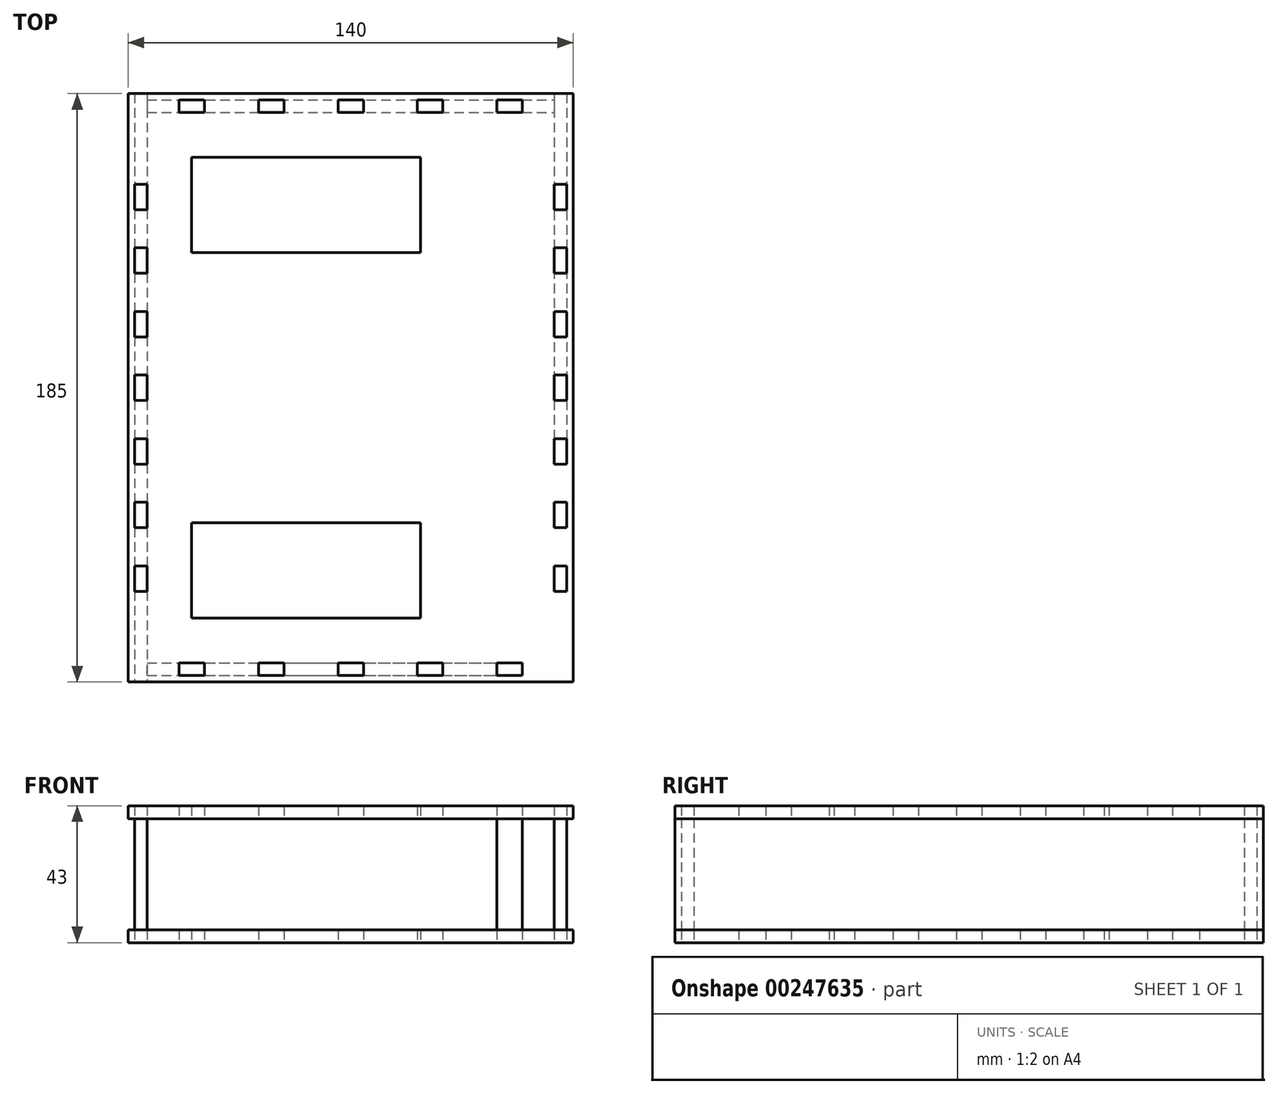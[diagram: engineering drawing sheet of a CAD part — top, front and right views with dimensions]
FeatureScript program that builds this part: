
annotation { "Feature Type Name" : "Feature", "Feature Type Description" : "" }
export const myFeature = defineFeature(function(context is Context, id is Id, definition is map)
    precondition{}
    {
        {
            var Q0;
            Q0=qCreatedBy(makeId("Top.planeOp"),FACE);
            var sketch = newSketch(context, id + "F0", { "sketchPlane" : qUnion([Q0])});
            skLineSegment(sketch, "E0.bottom", {"start": v(70, -92.5) * mm, "end": v(-70, -92.5) * mm});
            skLineSegment(sketch, "E0.top", {"start": v(70, 92.5) * mm, "end": v(-70, 92.5) * mm});
            skLineSegment(sketch, "E0.left", {"start": v(70, -92.5) * mm, "end": v(70, 92.5) * mm});
            skLineSegment(sketch, "E0.right", {"start": v(-70, -92.5) * mm, "end": v(-70, 92.5) * mm});
            skPoint(sketch, "E0.middle", {"position": v(0, 0) * mm});
            skPoint(sketch, "E1", {"position": v(0, 90.5) * mm});
            skLineSegment(sketch, "E2.bottom", {"start": v(0, 90.5) * mm, "end": v(4, 90.5) * mm});
            skLineSegment(sketch, "E2.top", {"start": v(0, 86.5) * mm, "end": v(4, 86.5) * mm});
            skLineSegment(sketch, "E2.left", {"start": v(0, 90.5) * mm, "end": v(0, 86.5) * mm});
            skLineSegment(sketch, "E2.right", {"start": v(4, 90.5) * mm, "end": v(4, 86.5) * mm});
            skLineSegment(sketch, "E3.MirrorCS", {"start": v(-4, 90.5) * mm, "end": v(-4, 86.5) * mm});
            skLineSegment(sketch, "E4.MirrorCS", {"start": v(0, 90.5) * mm, "end": v(-4, 90.5) * mm});
            skLineSegment(sketch, "E5.MirrorCS", {"start": v(0, 86.5) * mm, "end": v(-4, 86.5) * mm});
            skLineSegment(sketch, "E6.1.0.0", {"start": v(25, 86.5) * mm, "end": v(21, 86.5) * mm});
            skLineSegment(sketch, "E6.1.0.1", {"start": v(21, 90.5) * mm, "end": v(21, 86.5) * mm});
            skLineSegment(sketch, "E6.1.0.2", {"start": v(25, 90.5) * mm, "end": v(21, 90.5) * mm});
            skLineSegment(sketch, "E6.1.0.3", {"start": v(25, 90.5) * mm, "end": v(29, 90.5) * mm});
            skLineSegment(sketch, "E6.1.0.4", {"start": v(25, 86.5) * mm, "end": v(29, 86.5) * mm});
            skLineSegment(sketch, "E6.1.0.5", {"start": v(29, 90.5) * mm, "end": v(29, 86.5) * mm});
            skLineSegment(sketch, "E6.2.0.0", {"start": v(50, 86.5) * mm, "end": v(46, 86.5) * mm});
            skLineSegment(sketch, "E6.2.0.1", {"start": v(46, 90.5) * mm, "end": v(46, 86.5) * mm});
            skLineSegment(sketch, "E6.2.0.2", {"start": v(50, 90.5) * mm, "end": v(46, 90.5) * mm});
            skLineSegment(sketch, "E6.2.0.3", {"start": v(50, 90.5) * mm, "end": v(54, 90.5) * mm});
            skLineSegment(sketch, "E6.2.0.4", {"start": v(50, 86.5) * mm, "end": v(54, 86.5) * mm});
            skLineSegment(sketch, "E6.2.0.5", {"start": v(54, 90.5) * mm, "end": v(54, 86.5) * mm});
            skLineSegment(sketch, "E6.direction1", {"start": v(-4, 86.5) * mm, "end": v(21, 86.5) * mm, "construction": true});
            skLineSegment(sketch, "E7.MirrorCS", {"start": v(-25, 90.5) * mm, "end": v(-21, 90.5) * mm});
            skLineSegment(sketch, "E8.MirrorCS", {"start": v(-25, 90.5) * mm, "end": v(-29, 90.5) * mm});
            skLineSegment(sketch, "E9.MirrorCS", {"start": v(-29, 90.5) * mm, "end": v(-29, 86.5) * mm});
            skLineSegment(sketch, "E10.MirrorCS", {"start": v(-21, 90.5) * mm, "end": v(-21, 86.5) * mm});
            skLineSegment(sketch, "E11.MirrorCS", {"start": v(-25, 86.5) * mm, "end": v(-21, 86.5) * mm});
            skLineSegment(sketch, "E12.MirrorCS", {"start": v(-25, 86.5) * mm, "end": v(-29, 86.5) * mm});
            skLineSegment(sketch, "E13.MirrorCS", {"start": v(-50, 90.5) * mm, "end": v(-46, 90.5) * mm});
            skLineSegment(sketch, "E14.MirrorCS", {"start": v(-50, 90.5) * mm, "end": v(-54, 90.5) * mm});
            skLineSegment(sketch, "E15.MirrorCS", {"start": v(-54, 90.5) * mm, "end": v(-54, 86.5) * mm});
            skLineSegment(sketch, "E16.MirrorCS", {"start": v(-50, 86.5) * mm, "end": v(-54, 86.5) * mm});
            skLineSegment(sketch, "E17.MirrorCS", {"start": v(-50, 86.5) * mm, "end": v(-46, 86.5) * mm});
            skLineSegment(sketch, "E18.MirrorCS", {"start": v(-46, 90.5) * mm, "end": v(-46, 86.5) * mm});
            skLineSegment(sketch, "E19", {"start": v(-70, 0) * mm, "end": v(70, 0) * mm, "construction": true});
            skPoint(sketch, "E20", {"position": v(-68, 0) * mm});
            skLineSegment(sketch, "E21.bottom", {"start": v(-68, 0) * mm, "end": v(-64, 0) * mm});
            skLineSegment(sketch, "E21.top", {"start": v(-68, 4) * mm, "end": v(-64, 4) * mm});
            skLineSegment(sketch, "E21.left", {"start": v(-68, 0) * mm, "end": v(-68, 4) * mm});
            skLineSegment(sketch, "E21.right", {"start": v(-64, 0) * mm, "end": v(-64, 4) * mm});
            skLineSegment(sketch, "E22.MirrorCS", {"start": v(-68, -4) * mm, "end": v(-64, -4) * mm});
            skLineSegment(sketch, "E23.MirrorCS", {"start": v(-68, 0) * mm, "end": v(-68, -4) * mm});
            skLineSegment(sketch, "E24.MirrorCS", {"start": v(-64, 0) * mm, "end": v(-64, -4) * mm});
            skLineSegment(sketch, "E25.0.1.0", {"start": v(-68, 24) * mm, "end": v(-64, 24) * mm});
            skLineSegment(sketch, "E25.0.1.1", {"start": v(-68, 20) * mm, "end": v(-68, 24) * mm});
            skLineSegment(sketch, "E25.0.1.2", {"start": v(-64, 20) * mm, "end": v(-64, 24) * mm});
            skLineSegment(sketch, "E25.0.1.3", {"start": v(-64, 20) * mm, "end": v(-64, 16) * mm});
            skLineSegment(sketch, "E25.0.1.4", {"start": v(-68, 16) * mm, "end": v(-64, 16) * mm});
            skLineSegment(sketch, "E25.0.1.5", {"start": v(-68, 20) * mm, "end": v(-68, 16) * mm});
            skLineSegment(sketch, "E25.0.2.0", {"start": v(-68, 44) * mm, "end": v(-64, 44) * mm});
            skLineSegment(sketch, "E25.0.2.1", {"start": v(-68, 40) * mm, "end": v(-68, 44) * mm});
            skLineSegment(sketch, "E25.0.2.2", {"start": v(-64, 40) * mm, "end": v(-64, 44) * mm});
            skLineSegment(sketch, "E25.0.2.3", {"start": v(-64, 40) * mm, "end": v(-64, 36) * mm});
            skLineSegment(sketch, "E25.0.2.4", {"start": v(-68, 36) * mm, "end": v(-64, 36) * mm});
            skLineSegment(sketch, "E25.0.2.5", {"start": v(-68, 40) * mm, "end": v(-68, 36) * mm});
            skLineSegment(sketch, "E25.0.3.0", {"start": v(-68, 64) * mm, "end": v(-64, 64) * mm});
            skLineSegment(sketch, "E25.0.3.1", {"start": v(-68, 60) * mm, "end": v(-68, 64) * mm});
            skLineSegment(sketch, "E25.0.3.2", {"start": v(-64, 60) * mm, "end": v(-64, 64) * mm});
            skLineSegment(sketch, "E25.0.3.3", {"start": v(-64, 60) * mm, "end": v(-64, 56) * mm});
            skLineSegment(sketch, "E25.0.3.4", {"start": v(-68, 56) * mm, "end": v(-64, 56) * mm});
            skLineSegment(sketch, "E25.0.3.5", {"start": v(-68, 60) * mm, "end": v(-68, 56) * mm});
            skLineSegment(sketch, "E25.direction1", {"start": v(-68, 4) * mm, "end": v(-43, 4) * mm, "construction": true});
            skLineSegment(sketch, "E25.direction2", {"start": v(-68, 4) * mm, "end": v(-68, 24) * mm, "construction": true});
            skLineSegment(sketch, "E26.MirrorCS", {"start": v(-68, -24) * mm, "end": v(-64, -24) * mm});
            skLineSegment(sketch, "E27.MirrorCS", {"start": v(-64, -20) * mm, "end": v(-64, -24) * mm});
            skLineSegment(sketch, "E28.MirrorCS", {"start": v(-64, -20) * mm, "end": v(-64, -16) * mm});
            skLineSegment(sketch, "E29.MirrorCS", {"start": v(-68, -16) * mm, "end": v(-64, -16) * mm});
            skLineSegment(sketch, "E30.MirrorCS", {"start": v(-68, -36) * mm, "end": v(-64, -36) * mm});
            skLineSegment(sketch, "E31.MirrorCS", {"start": v(-68, -40) * mm, "end": v(-68, -36) * mm});
            skLineSegment(sketch, "E32.MirrorCS", {"start": v(-68, -40) * mm, "end": v(-68, -44) * mm});
            skLineSegment(sketch, "E33.MirrorCS", {"start": v(-68, -44) * mm, "end": v(-64, -44) * mm});
            skLineSegment(sketch, "E34.MirrorCS", {"start": v(-64, -40) * mm, "end": v(-64, -44) * mm});
            skLineSegment(sketch, "E35.MirrorCS", {"start": v(-64, -40) * mm, "end": v(-64, -36) * mm});
            skLineSegment(sketch, "E36.MirrorCS", {"start": v(-68, -64) * mm, "end": v(-64, -64) * mm});
            skLineSegment(sketch, "E37.MirrorCS", {"start": v(-68, -60) * mm, "end": v(-68, -64) * mm});
            skLineSegment(sketch, "E38.MirrorCS", {"start": v(-64, -60) * mm, "end": v(-64, -64) * mm});
            skLineSegment(sketch, "E39.MirrorCS", {"start": v(-64, -60) * mm, "end": v(-64, -56) * mm});
            skLineSegment(sketch, "E40.MirrorCS", {"start": v(-68, -60) * mm, "end": v(-68, -56) * mm});
            skLineSegment(sketch, "E41.MirrorCS", {"start": v(-68, -56) * mm, "end": v(-64, -56) * mm});
            skLineSegment(sketch, "E42", {"start": v(-68, -16) * mm, "end": v(-68, -24) * mm});
            skLineSegment(sketch, "E43.MirrorCS", {"start": v(68, 64) * mm, "end": v(64, 64) * mm});
            skLineSegment(sketch, "E44.MirrorCS", {"start": v(64, 60) * mm, "end": v(64, 64) * mm});
            skLineSegment(sketch, "E45.MirrorCS", {"start": v(68, 60) * mm, "end": v(68, 64) * mm});
            skLineSegment(sketch, "E46.MirrorCS", {"start": v(68, 60) * mm, "end": v(68, 56) * mm});
            skLineSegment(sketch, "E47.MirrorCS", {"start": v(64, 60) * mm, "end": v(64, 56) * mm});
            skLineSegment(sketch, "E48.MirrorCS", {"start": v(68, 56) * mm, "end": v(64, 56) * mm});
            skLineSegment(sketch, "E49.MirrorCS", {"start": v(68, 44) * mm, "end": v(64, 44) * mm});
            skLineSegment(sketch, "E50.MirrorCS", {"start": v(64, 40) * mm, "end": v(64, 44) * mm});
            skLineSegment(sketch, "E51.MirrorCS", {"start": v(64, 40) * mm, "end": v(64, 36) * mm});
            skLineSegment(sketch, "E52.MirrorCS", {"start": v(68, 36) * mm, "end": v(64, 36) * mm});
            skLineSegment(sketch, "E53.MirrorCS", {"start": v(68, 40) * mm, "end": v(68, 36) * mm});
            skLineSegment(sketch, "E54.MirrorCS", {"start": v(68, 40) * mm, "end": v(68, 44) * mm});
            skLineSegment(sketch, "E55.MirrorCS", {"start": v(68, 24) * mm, "end": v(64, 24) * mm});
            skLineSegment(sketch, "E56.MirrorCS", {"start": v(64, 20) * mm, "end": v(64, 24) * mm});
            skLineSegment(sketch, "E57.MirrorCS", {"start": v(64, 20) * mm, "end": v(64, 16) * mm});
            skLineSegment(sketch, "E58.MirrorCS", {"start": v(68, 16) * mm, "end": v(64, 16) * mm});
            skLineSegment(sketch, "E59.MirrorCS", {"start": v(68, 0) * mm, "end": v(68, 4) * mm});
            skLineSegment(sketch, "E60.MirrorCS", {"start": v(68, 0) * mm, "end": v(68, -4) * mm});
            skLineSegment(sketch, "E61.MirrorCS", {"start": v(68, -4) * mm, "end": v(64, -4) * mm});
            skLineSegment(sketch, "E62.MirrorCS", {"start": v(64, 0) * mm, "end": v(64, -4) * mm});
            skLineSegment(sketch, "E63.MirrorCS", {"start": v(64, 0) * mm, "end": v(64, 4) * mm});
            skLineSegment(sketch, "E64.MirrorCS", {"start": v(68, -16) * mm, "end": v(64, -16) * mm});
            skLineSegment(sketch, "E65.MirrorCS", {"start": v(68, -16) * mm, "end": v(68, -24) * mm});
            skLineSegment(sketch, "E66.MirrorCS", {"start": v(64, -20) * mm, "end": v(64, -16) * mm});
            skLineSegment(sketch, "E67.MirrorCS", {"start": v(64, -20) * mm, "end": v(64, -24) * mm});
            skLineSegment(sketch, "E68.MirrorCS", {"start": v(68, -24) * mm, "end": v(64, -24) * mm});
            skLineSegment(sketch, "E69.MirrorCS", {"start": v(68, -36) * mm, "end": v(64, -36) * mm});
            skLineSegment(sketch, "E70.MirrorCS", {"start": v(68, -40) * mm, "end": v(68, -36) * mm});
            skLineSegment(sketch, "E71.MirrorCS", {"start": v(64, -40) * mm, "end": v(64, -36) * mm});
            skLineSegment(sketch, "E72.MirrorCS", {"start": v(64, -40) * mm, "end": v(64, -44) * mm});
            skLineSegment(sketch, "E73.MirrorCS", {"start": v(68, -40) * mm, "end": v(68, -44) * mm});
            skLineSegment(sketch, "E74.MirrorCS", {"start": v(68, -44) * mm, "end": v(64, -44) * mm});
            skLineSegment(sketch, "E75.MirrorCS", {"start": v(68, -56) * mm, "end": v(64, -56) * mm});
            skLineSegment(sketch, "E76.MirrorCS", {"start": v(68, -60) * mm, "end": v(68, -56) * mm});
            skLineSegment(sketch, "E77.MirrorCS", {"start": v(64, -60) * mm, "end": v(64, -56) * mm});
            skLineSegment(sketch, "E78.MirrorCS", {"start": v(64, -60) * mm, "end": v(64, -64) * mm});
            skLineSegment(sketch, "E79.MirrorCS", {"start": v(68, -64) * mm, "end": v(64, -64) * mm});
            skLineSegment(sketch, "E80.MirrorCS", {"start": v(68, -60) * mm, "end": v(68, -64) * mm});
            skLineSegment(sketch, "E81", {"start": v(64, 4) * mm, "end": v(68, 4) * mm});
            skLineSegment(sketch, "E82", {"start": v(68, 24) * mm, "end": v(68, 16) * mm});
            skLineSegment(sketch, "E83.MirrorCS", {"start": v(-50, -90.5) * mm, "end": v(-54, -90.5) * mm});
            skLineSegment(sketch, "E84.MirrorCS", {"start": v(-50, -90.5) * mm, "end": v(-46, -90.5) * mm});
            skLineSegment(sketch, "E85.MirrorCS", {"start": v(-46, -90.5) * mm, "end": v(-46, -86.5) * mm});
            skLineSegment(sketch, "E86.MirrorCS", {"start": v(-50, -86.5) * mm, "end": v(-46, -86.5) * mm});
            skLineSegment(sketch, "E87.MirrorCS", {"start": v(-50, -86.5) * mm, "end": v(-54, -86.5) * mm});
            skLineSegment(sketch, "E88.MirrorCS", {"start": v(-54, -90.5) * mm, "end": v(-54, -86.5) * mm});
            skLineSegment(sketch, "E89.MirrorCS", {"start": v(-25, -90.5) * mm, "end": v(-29, -90.5) * mm});
            skLineSegment(sketch, "E90.MirrorCS", {"start": v(-25, -90.5) * mm, "end": v(-21, -90.5) * mm});
            skLineSegment(sketch, "E91.MirrorCS", {"start": v(-21, -90.5) * mm, "end": v(-21, -86.5) * mm});
            skLineSegment(sketch, "E92.MirrorCS", {"start": v(-25, -86.5) * mm, "end": v(-21, -86.5) * mm});
            skLineSegment(sketch, "E93.MirrorCS", {"start": v(-25, -86.5) * mm, "end": v(-29, -86.5) * mm});
            skLineSegment(sketch, "E94.MirrorCS", {"start": v(-29, -90.5) * mm, "end": v(-29, -86.5) * mm});
            skLineSegment(sketch, "E95.MirrorCS", {"start": v(0, -90.5) * mm, "end": v(-4, -90.5) * mm});
            skLineSegment(sketch, "E96.MirrorCS", {"start": v(0, -90.5) * mm, "end": v(4, -90.5) * mm});
            skLineSegment(sketch, "E97.MirrorCS", {"start": v(4, -90.5) * mm, "end": v(4, -86.5) * mm});
            skLineSegment(sketch, "E98.MirrorCS", {"start": v(-4, -90.5) * mm, "end": v(-4, -86.5) * mm});
            skLineSegment(sketch, "E99.MirrorCS", {"start": v(25, -90.5) * mm, "end": v(21, -90.5) * mm});
            skLineSegment(sketch, "E100.MirrorCS", {"start": v(25, -90.5) * mm, "end": v(29, -90.5) * mm});
            skLineSegment(sketch, "E101.MirrorCS", {"start": v(29, -90.5) * mm, "end": v(29, -86.5) * mm});
            skLineSegment(sketch, "E102.MirrorCS", {"start": v(25, -86.5) * mm, "end": v(29, -86.5) * mm});
            skLineSegment(sketch, "E103.MirrorCS", {"start": v(25, -86.5) * mm, "end": v(21, -86.5) * mm});
            skLineSegment(sketch, "E104.MirrorCS", {"start": v(21, -90.5) * mm, "end": v(21, -86.5) * mm});
            skLineSegment(sketch, "E105.MirrorCS", {"start": v(50, -90.5) * mm, "end": v(46, -90.5) * mm});
            skLineSegment(sketch, "E106.MirrorCS", {"start": v(50, -90.5) * mm, "end": v(54, -90.5) * mm});
            skLineSegment(sketch, "E107.MirrorCS", {"start": v(54, -90.5) * mm, "end": v(54, -86.5) * mm});
            skLineSegment(sketch, "E108.MirrorCS", {"start": v(50, -86.5) * mm, "end": v(54, -86.5) * mm});
            skLineSegment(sketch, "E109.MirrorCS", {"start": v(50, -86.5) * mm, "end": v(46, -86.5) * mm});
            skLineSegment(sketch, "E110.MirrorCS", {"start": v(46, -90.5) * mm, "end": v(46, -86.5) * mm});
            skLineSegment(sketch, "E111", {"start": v(-4, -86.5) * mm, "end": v(4, -86.5) * mm});
            skLineSegment(sketch, "E112", {"start": v(-50, -42.5) * mm, "end": v(-50, -72.5) * mm});
            skLineSegment(sketch, "E113", {"start": v(22, -42.5) * mm, "end": v(22, -72.5) * mm});
            skLineSegment(sketch, "E114", {"start": v(-50, -42.5) * mm, "end": v(22, -42.5) * mm});
            skLineSegment(sketch, "E115", {"start": v(-50, -72.5) * mm, "end": v(22, -72.5) * mm});
            skLineSegment(sketch, "E116", {"start": v(0, -92.5) * mm, "end": v(0, 92.5) * mm, "construction": true});
            skLineSegment(sketch, "E117.MirrorCS", {"start": v(-50, 42.5) * mm, "end": v(-50, 72.5) * mm});
            skLineSegment(sketch, "E118.MirrorCS", {"start": v(-50, 72.5) * mm, "end": v(22, 72.5) * mm});
            skLineSegment(sketch, "E119.MirrorCS", {"start": v(-50, 42.5) * mm, "end": v(22, 42.5) * mm});
            skLineSegment(sketch, "E120.MirrorCS", {"start": v(22, 42.5) * mm, "end": v(22, 72.5) * mm});
            skSolve(sketch);
        }
        {
            var Q0;
            Q0=makeQuery(id+"F0.imprint","IMPRINT",FACE,{"disambiguationData":[TD([[makeQuery(id+"F0.imprint","IMPRINT",EDGE,{"derivedFrom":sQuery(id+"F0.wireOp",EDGE,"E0.bottom")}),-1.0]])]});
            extrude(context, id + "F1", {"entities" : qUnion([Q0]), "depth" : 4 * mm});
        }
        {
            var Q0;
            Q0=makeQuery(id+"F1.opExtrude","CAP_FACE",FACE,{"disambiguationData":[OSD([sQuery(id+"F0.wireOp",EDGE,"E0.bottom"),sQuery(id+"F0.wireOp",EDGE,"E0.top"),sQuery(id+"F0.wireOp",EDGE,"E0.left"),sQuery(id+"F0.wireOp",EDGE,"E0.right"),sQuery(id+"F0.wireOp",EDGE,"E2.bottom"),sQuery(id+"F0.wireOp",EDGE,"E2.top"),sQuery(id+"F0.wireOp",EDGE,"E2.right"),sQuery(id+"F0.wireOp",EDGE,"E3.MirrorCS"),sQuery(id+"F0.wireOp",EDGE,"E4.MirrorCS"),sQuery(id+"F0.wireOp",EDGE,"E5.MirrorCS"),sQuery(id+"F0.wireOp",EDGE,"E6.1.0.0"),sQuery(id+"F0.wireOp",EDGE,"E6.1.0.1"),sQuery(id+"F0.wireOp",EDGE,"E6.1.0.2"),sQuery(id+"F0.wireOp",EDGE,"E6.1.0.3"),sQuery(id+"F0.wireOp",EDGE,"E6.1.0.4"),sQuery(id+"F0.wireOp",EDGE,"E6.1.0.5"),sQuery(id+"F0.wireOp",EDGE,"E6.2.0.0"),sQuery(id+"F0.wireOp",EDGE,"E6.2.0.1"),sQuery(id+"F0.wireOp",EDGE,"E6.2.0.2"),sQuery(id+"F0.wireOp",EDGE,"E6.2.0.3"),sQuery(id+"F0.wireOp",EDGE,"E6.2.0.4"),sQuery(id+"F0.wireOp",EDGE,"E6.2.0.5"),sQuery(id+"F0.wireOp",EDGE,"E7.MirrorCS"),sQuery(id+"F0.wireOp",EDGE,"E8.MirrorCS"),sQuery(id+"F0.wireOp",EDGE,"E9.MirrorCS"),sQuery(id+"F0.wireOp",EDGE,"E10.MirrorCS"),sQuery(id+"F0.wireOp",EDGE,"E11.MirrorCS"),sQuery(id+"F0.wireOp",EDGE,"E12.MirrorCS"),sQuery(id+"F0.wireOp",EDGE,"E13.MirrorCS"),sQuery(id+"F0.wireOp",EDGE,"E14.MirrorCS"),sQuery(id+"F0.wireOp",EDGE,"E15.MirrorCS"),sQuery(id+"F0.wireOp",EDGE,"E16.MirrorCS"),sQuery(id+"F0.wireOp",EDGE,"E17.MirrorCS"),sQuery(id+"F0.wireOp",EDGE,"E18.MirrorCS"),sQuery(id+"F0.wireOp",EDGE,"E21.top"),sQuery(id+"F0.wireOp",EDGE,"E21.left"),sQuery(id+"F0.wireOp",EDGE,"E21.right"),sQuery(id+"F0.wireOp",EDGE,"E22.MirrorCS"),sQuery(id+"F0.wireOp",EDGE,"E23.MirrorCS"),sQuery(id+"F0.wireOp",EDGE,"E24.MirrorCS"),sQuery(id+"F0.wireOp",EDGE,"E25.0.1.0"),sQuery(id+"F0.wireOp",EDGE,"E25.0.1.1"),sQuery(id+"F0.wireOp",EDGE,"E25.0.1.2"),sQuery(id+"F0.wireOp",EDGE,"E25.0.1.3"),sQuery(id+"F0.wireOp",EDGE,"E25.0.1.4"),sQuery(id+"F0.wireOp",EDGE,"E25.0.1.5"),sQuery(id+"F0.wireOp",EDGE,"E25.0.2.0"),sQuery(id+"F0.wireOp",EDGE,"E25.0.2.1"),sQuery(id+"F0.wireOp",EDGE,"E25.0.2.2"),sQuery(id+"F0.wireOp",EDGE,"E25.0.2.3"),sQuery(id+"F0.wireOp",EDGE,"E25.0.2.4"),sQuery(id+"F0.wireOp",EDGE,"E25.0.2.5"),sQuery(id+"F0.wireOp",EDGE,"E25.0.3.0"),sQuery(id+"F0.wireOp",EDGE,"E25.0.3.1"),sQuery(id+"F0.wireOp",EDGE,"E25.0.3.2"),sQuery(id+"F0.wireOp",EDGE,"E25.0.3.3"),sQuery(id+"F0.wireOp",EDGE,"E25.0.3.4"),sQuery(id+"F0.wireOp",EDGE,"E25.0.3.5"),sQuery(id+"F0.wireOp",EDGE,"E26.MirrorCS"),sQuery(id+"F0.wireOp",EDGE,"E27.MirrorCS"),sQuery(id+"F0.wireOp",EDGE,"E28.MirrorCS"),sQuery(id+"F0.wireOp",EDGE,"E29.MirrorCS"),sQuery(id+"F0.wireOp",EDGE,"E30.MirrorCS"),sQuery(id+"F0.wireOp",EDGE,"E31.MirrorCS"),sQuery(id+"F0.wireOp",EDGE,"E32.MirrorCS"),sQuery(id+"F0.wireOp",EDGE,"E33.MirrorCS"),sQuery(id+"F0.wireOp",EDGE,"E34.MirrorCS"),sQuery(id+"F0.wireOp",EDGE,"E35.MirrorCS"),sQuery(id+"F0.wireOp",EDGE,"E36.MirrorCS"),sQuery(id+"F0.wireOp",EDGE,"E37.MirrorCS"),sQuery(id+"F0.wireOp",EDGE,"E38.MirrorCS"),sQuery(id+"F0.wireOp",EDGE,"E39.MirrorCS"),sQuery(id+"F0.wireOp",EDGE,"E40.MirrorCS"),sQuery(id+"F0.wireOp",EDGE,"E41.MirrorCS"),sQuery(id+"F0.wireOp",EDGE,"E42"),sQuery(id+"F0.wireOp",EDGE,"E43.MirrorCS"),sQuery(id+"F0.wireOp",EDGE,"E44.MirrorCS"),sQuery(id+"F0.wireOp",EDGE,"E45.MirrorCS"),sQuery(id+"F0.wireOp",EDGE,"E46.MirrorCS"),sQuery(id+"F0.wireOp",EDGE,"E47.MirrorCS"),sQuery(id+"F0.wireOp",EDGE,"E48.MirrorCS"),sQuery(id+"F0.wireOp",EDGE,"E49.MirrorCS"),sQuery(id+"F0.wireOp",EDGE,"E50.MirrorCS"),sQuery(id+"F0.wireOp",EDGE,"E51.MirrorCS"),sQuery(id+"F0.wireOp",EDGE,"E52.MirrorCS"),sQuery(id+"F0.wireOp",EDGE,"E53.MirrorCS"),sQuery(id+"F0.wireOp",EDGE,"E54.MirrorCS"),sQuery(id+"F0.wireOp",EDGE,"E55.MirrorCS"),sQuery(id+"F0.wireOp",EDGE,"E56.MirrorCS"),sQuery(id+"F0.wireOp",EDGE,"E57.MirrorCS"),sQuery(id+"F0.wireOp",EDGE,"E58.MirrorCS"),sQuery(id+"F0.wireOp",EDGE,"E59.MirrorCS"),sQuery(id+"F0.wireOp",EDGE,"E60.MirrorCS"),sQuery(id+"F0.wireOp",EDGE,"E61.MirrorCS"),sQuery(id+"F0.wireOp",EDGE,"E62.MirrorCS"),sQuery(id+"F0.wireOp",EDGE,"E63.MirrorCS"),sQuery(id+"F0.wireOp",EDGE,"E64.MirrorCS"),sQuery(id+"F0.wireOp",EDGE,"E65.MirrorCS"),sQuery(id+"F0.wireOp",EDGE,"E66.MirrorCS"),sQuery(id+"F0.wireOp",EDGE,"E67.MirrorCS"),sQuery(id+"F0.wireOp",EDGE,"E68.MirrorCS"),sQuery(id+"F0.wireOp",EDGE,"E69.MirrorCS"),sQuery(id+"F0.wireOp",EDGE,"E70.MirrorCS"),sQuery(id+"F0.wireOp",EDGE,"E71.MirrorCS"),sQuery(id+"F0.wireOp",EDGE,"E72.MirrorCS"),sQuery(id+"F0.wireOp",EDGE,"E73.MirrorCS"),sQuery(id+"F0.wireOp",EDGE,"E74.MirrorCS"),sQuery(id+"F0.wireOp",EDGE,"E75.MirrorCS"),sQuery(id+"F0.wireOp",EDGE,"E76.MirrorCS"),sQuery(id+"F0.wireOp",EDGE,"E77.MirrorCS"),sQuery(id+"F0.wireOp",EDGE,"E78.MirrorCS"),sQuery(id+"F0.wireOp",EDGE,"E79.MirrorCS"),sQuery(id+"F0.wireOp",EDGE,"E80.MirrorCS"),sQuery(id+"F0.wireOp",EDGE,"E81"),sQuery(id+"F0.wireOp",EDGE,"E82"),sQuery(id+"F0.wireOp",EDGE,"E83.MirrorCS"),sQuery(id+"F0.wireOp",EDGE,"E84.MirrorCS"),sQuery(id+"F0.wireOp",EDGE,"E85.MirrorCS"),sQuery(id+"F0.wireOp",EDGE,"E86.MirrorCS"),sQuery(id+"F0.wireOp",EDGE,"E87.MirrorCS"),sQuery(id+"F0.wireOp",EDGE,"E88.MirrorCS"),sQuery(id+"F0.wireOp",EDGE,"E89.MirrorCS"),sQuery(id+"F0.wireOp",EDGE,"E90.MirrorCS"),sQuery(id+"F0.wireOp",EDGE,"E91.MirrorCS"),sQuery(id+"F0.wireOp",EDGE,"E92.MirrorCS"),sQuery(id+"F0.wireOp",EDGE,"E93.MirrorCS"),sQuery(id+"F0.wireOp",EDGE,"E94.MirrorCS"),sQuery(id+"F0.wireOp",EDGE,"E95.MirrorCS"),sQuery(id+"F0.wireOp",EDGE,"E96.MirrorCS"),sQuery(id+"F0.wireOp",EDGE,"E97.MirrorCS"),sQuery(id+"F0.wireOp",EDGE,"E98.MirrorCS"),sQuery(id+"F0.wireOp",EDGE,"E99.MirrorCS"),sQuery(id+"F0.wireOp",EDGE,"E100.MirrorCS"),sQuery(id+"F0.wireOp",EDGE,"E101.MirrorCS"),sQuery(id+"F0.wireOp",EDGE,"E102.MirrorCS"),sQuery(id+"F0.wireOp",EDGE,"E103.MirrorCS"),sQuery(id+"F0.wireOp",EDGE,"E104.MirrorCS"),sQuery(id+"F0.wireOp",EDGE,"E105.MirrorCS"),sQuery(id+"F0.wireOp",EDGE,"E106.MirrorCS"),sQuery(id+"F0.wireOp",EDGE,"E107.MirrorCS"),sQuery(id+"F0.wireOp",EDGE,"E108.MirrorCS"),sQuery(id+"F0.wireOp",EDGE,"E109.MirrorCS"),sQuery(id+"F0.wireOp",EDGE,"E110.MirrorCS"),sQuery(id+"F0.wireOp",EDGE,"E111")])],"isStart":false});
            cPlane(context, id + "F2", {"entities" : qUnion([Q0]), "cplaneType" : CPlaneType.OFFSET, "offset" : 35 * mm, "width" : 150 * mm, "height" : 150 * mm});
        }
        {
            var Q0;
            Q0=qCreatedBy(id+"F2.planeOp",FACE);
            var sketch = newSketch(context, id + "F3", { "sketchPlane" : qUnion([Q0])});
            skLineSegment(sketch, "E121.0.0", {"start": v(70, -92.5) * mm, "end": v(70, 92.5) * mm});
            skLineSegment(sketch, "E121.0.1", {"start": v(70, 92.5) * mm, "end": v(-70, 92.5) * mm});
            skLineSegment(sketch, "E121.0.2", {"start": v(-70, 92.5) * mm, "end": v(-70, -92.5) * mm});
            skLineSegment(sketch, "E121.0.3", {"start": v(-70, -92.5) * mm, "end": v(70, -92.5) * mm});
            skLineSegment(sketch, "E122.0", {"start": v(-46, -86.5) * mm, "end": v(-54, -86.5) * mm});
            skLineSegment(sketch, "E123.0", {"start": v(-46, -90.5) * mm, "end": v(-46, -86.5) * mm});
            skLineSegment(sketch, "E124.0", {"start": v(-46, -90.5) * mm, "end": v(-54, -90.5) * mm});
            skLineSegment(sketch, "E125.0", {"start": v(-54, -90.5) * mm, "end": v(-54, -86.5) * mm});
            skLineSegment(sketch, "E126.0", {"start": v(-21, -86.5) * mm, "end": v(-29, -86.5) * mm});
            skLineSegment(sketch, "E127.0", {"start": v(-21, -90.5) * mm, "end": v(-21, -86.5) * mm});
            skLineSegment(sketch, "E128.0", {"start": v(-21, -90.5) * mm, "end": v(-29, -90.5) * mm});
            skLineSegment(sketch, "E129.0", {"start": v(-29, -90.5) * mm, "end": v(-29, -86.5) * mm});
            skPoint(sketch, "E130.0", {"position": v(0, -86.5) * mm});
            skLineSegment(sketch, "E131.0", {"start": v(-4, -86.5) * mm, "end": v(4, -86.5) * mm});
            skLineSegment(sketch, "E132.0", {"start": v(-4, -90.5) * mm, "end": v(-4, -86.5) * mm});
            skLineSegment(sketch, "E133.0", {"start": v(-4, -90.5) * mm, "end": v(4, -90.5) * mm});
            skLineSegment(sketch, "E134.0", {"start": v(4, -90.5) * mm, "end": v(4, -86.5) * mm});
            skLineSegment(sketch, "E135.0", {"start": v(29, -86.5) * mm, "end": v(21, -86.5) * mm});
            skLineSegment(sketch, "E136.0", {"start": v(21, -90.5) * mm, "end": v(21, -86.5) * mm});
            skLineSegment(sketch, "E137.0", {"start": v(29, -90.5) * mm, "end": v(21, -90.5) * mm});
            skLineSegment(sketch, "E138.0", {"start": v(29, -90.5) * mm, "end": v(29, -86.5) * mm});
            skLineSegment(sketch, "E139.0", {"start": v(54, -86.5) * mm, "end": v(46, -86.5) * mm});
            skLineSegment(sketch, "E140.0", {"start": v(46, -90.5) * mm, "end": v(46, -86.5) * mm});
            skLineSegment(sketch, "E141.0", {"start": v(54, -90.5) * mm, "end": v(46, -90.5) * mm});
            skLineSegment(sketch, "E142.0", {"start": v(54, -90.5) * mm, "end": v(54, -86.5) * mm});
            skLineSegment(sketch, "E143.0.0", {"start": v(70, 92.5) * mm, "end": v(70, -92.5) * mm});
            skLineSegment(sketch, "E143.0.1", {"start": v(70, -92.5) * mm, "end": v(-70, -92.5) * mm});
            skLineSegment(sketch, "E143.0.2", {"start": v(-70, -92.5) * mm, "end": v(-70, 92.5) * mm});
            skLineSegment(sketch, "E143.0.3", {"start": v(-70, 92.5) * mm, "end": v(70, 92.5) * mm});
            skLineSegment(sketch, "E144.0", {"start": v(68, -56) * mm, "end": v(64, -56) * mm});
            skLineSegment(sketch, "E145.0", {"start": v(64, -56) * mm, "end": v(64, -64) * mm});
            skLineSegment(sketch, "E146.0", {"start": v(68, -64) * mm, "end": v(64, -64) * mm});
            skLineSegment(sketch, "E147.0", {"start": v(68, -64) * mm, "end": v(68, -56) * mm});
            skLineSegment(sketch, "E148.0", {"start": v(68, -36) * mm, "end": v(64, -36) * mm});
            skLineSegment(sketch, "E149.0", {"start": v(64, -36) * mm, "end": v(64, -44) * mm});
            skLineSegment(sketch, "E150.0", {"start": v(68, -44) * mm, "end": v(64, -44) * mm});
            skLineSegment(sketch, "E151.0", {"start": v(68, -36) * mm, "end": v(68, -44) * mm});
            skLineSegment(sketch, "E152.0", {"start": v(68, -16) * mm, "end": v(64, -16) * mm});
            skLineSegment(sketch, "E153.0.0", {"start": v(64, -24) * mm, "end": v(64, -16) * mm});
            skLineSegment(sketch, "E153.0.2", {"start": v(64, -16) * mm, "end": v(64, -24) * mm});
            skLineSegment(sketch, "E154.0", {"start": v(68, -24) * mm, "end": v(64, -24) * mm});
            skLineSegment(sketch, "E155.0", {"start": v(68, -16) * mm, "end": v(68, -24) * mm});
            skLineSegment(sketch, "E156.0", {"start": v(64, 4) * mm, "end": v(68, 4) * mm});
            skLineSegment(sketch, "E157.0.0", {"start": v(64, -4) * mm, "end": v(64, 4) * mm});
            skLineSegment(sketch, "E157.0.2", {"start": v(64, 4) * mm, "end": v(64, -4) * mm});
            skLineSegment(sketch, "E158.0", {"start": v(68, -4) * mm, "end": v(64, -4) * mm});
            skLineSegment(sketch, "E159.0", {"start": v(68, -4) * mm, "end": v(68, 4) * mm});
            skLineSegment(sketch, "E160.0", {"start": v(68, 24) * mm, "end": v(64, 24) * mm});
            skLineSegment(sketch, "E161.0", {"start": v(64, 24) * mm, "end": v(64, 16) * mm});
            skLineSegment(sketch, "E162.0", {"start": v(68, 16) * mm, "end": v(64, 16) * mm});
            skLineSegment(sketch, "E163.0", {"start": v(68, 24) * mm, "end": v(68, 16) * mm});
            skLineSegment(sketch, "E164.0", {"start": v(68, 44) * mm, "end": v(64, 44) * mm});
            skLineSegment(sketch, "E165.0", {"start": v(64, 44) * mm, "end": v(64, 36) * mm});
            skLineSegment(sketch, "E166.0", {"start": v(68, 36) * mm, "end": v(64, 36) * mm});
            skLineSegment(sketch, "E167.0", {"start": v(68, 36) * mm, "end": v(68, 44) * mm});
            skLineSegment(sketch, "E168.0", {"start": v(68, 64) * mm, "end": v(64, 64) * mm});
            skLineSegment(sketch, "E169.0", {"start": v(64, 64) * mm, "end": v(64, 56) * mm});
            skLineSegment(sketch, "E170.0", {"start": v(68, 56) * mm, "end": v(64, 56) * mm});
            skLineSegment(sketch, "E171.0", {"start": v(68, 64) * mm, "end": v(68, 56) * mm});
            skLineSegment(sketch, "E172.0", {"start": v(46, 90.5) * mm, "end": v(54, 90.5) * mm});
            skLineSegment(sketch, "E173.0", {"start": v(46, 90.5) * mm, "end": v(46, 86.5) * mm});
            skLineSegment(sketch, "E174.0", {"start": v(46, 86.5) * mm, "end": v(54, 86.5) * mm});
            skLineSegment(sketch, "E175.0", {"start": v(54, 90.5) * mm, "end": v(54, 86.5) * mm});
            skLineSegment(sketch, "E176.0", {"start": v(21, 90.5) * mm, "end": v(29, 90.5) * mm});
            skLineSegment(sketch, "E177.0", {"start": v(21, 90.5) * mm, "end": v(21, 86.5) * mm});
            skLineSegment(sketch, "E178.0", {"start": v(21, 86.5) * mm, "end": v(29, 86.5) * mm});
            skLineSegment(sketch, "E179.0", {"start": v(29, 90.5) * mm, "end": v(29, 86.5) * mm});
            skLineSegment(sketch, "E180.0", {"start": v(4, 90.5) * mm, "end": v(-4, 90.5) * mm});
            skLineSegment(sketch, "E181.0", {"start": v(-4, 90.5) * mm, "end": v(-4, 86.5) * mm});
            skLineSegment(sketch, "E182.0", {"start": v(-4, 86.5) * mm, "end": v(4, 86.5) * mm});
            skLineSegment(sketch, "E183.0", {"start": v(4, 90.5) * mm, "end": v(4, 86.5) * mm});
            skLineSegment(sketch, "E184.0", {"start": v(-21, 90.5) * mm, "end": v(-29, 90.5) * mm});
            skPoint(sketch, "E185.0", {"position": v(-29, 88.5) * mm});
            skPoint(sketch, "E186.0", {"position": v(-25, 86.5) * mm});
            skLineSegment(sketch, "E187.0", {"start": v(-29, 90.5) * mm, "end": v(-29, 86.5) * mm});
            skLineSegment(sketch, "E188.0", {"start": v(-21, 90.5) * mm, "end": v(-21, 86.5) * mm});
            skLineSegment(sketch, "E189.0", {"start": v(-54, 90.5) * mm, "end": v(-46, 90.5) * mm});
            skLineSegment(sketch, "E190.0", {"start": v(-54, 90.5) * mm, "end": v(-54, 86.5) * mm});
            skLineSegment(sketch, "E191.0", {"start": v(-54, 86.5) * mm, "end": v(-46, 86.5) * mm});
            skLineSegment(sketch, "E192.0", {"start": v(-46, 90.5) * mm, "end": v(-46, 86.5) * mm});
            skLineSegment(sketch, "E193.0", {"start": v(-68, 64) * mm, "end": v(-64, 64) * mm});
            skLineSegment(sketch, "E194.0", {"start": v(-68, 64) * mm, "end": v(-68, 56) * mm});
            skLineSegment(sketch, "E195.0", {"start": v(-68, 56) * mm, "end": v(-64, 56) * mm});
            skLineSegment(sketch, "E196.0", {"start": v(-64, 56) * mm, "end": v(-64, 64) * mm});
            skLineSegment(sketch, "E197.0", {"start": v(-68, 44) * mm, "end": v(-64, 44) * mm});
            skLineSegment(sketch, "E198.0", {"start": v(-68, 44) * mm, "end": v(-68, 36) * mm});
            skLineSegment(sketch, "E199.0", {"start": v(-68, 36) * mm, "end": v(-64, 36) * mm});
            skLineSegment(sketch, "E200.0", {"start": v(-64, 36) * mm, "end": v(-64, 44) * mm});
            skLineSegment(sketch, "E201.0", {"start": v(-68, 24) * mm, "end": v(-64, 24) * mm});
            skLineSegment(sketch, "E202.0", {"start": v(-68, 24) * mm, "end": v(-68, 16) * mm});
            skLineSegment(sketch, "E203.0", {"start": v(-64, 16) * mm, "end": v(-64, 24) * mm});
            skLineSegment(sketch, "E204.0", {"start": v(-68, 16) * mm, "end": v(-64, 16) * mm});
            skLineSegment(sketch, "E205.0", {"start": v(-68, 4) * mm, "end": v(-64, 4) * mm});
            skLineSegment(sketch, "E206.0", {"start": v(-68, 4) * mm, "end": v(-68, -4) * mm});
            skLineSegment(sketch, "E207.0", {"start": v(-64, -4) * mm, "end": v(-64, 4) * mm});
            skLineSegment(sketch, "E208.0", {"start": v(-68, -4) * mm, "end": v(-64, -4) * mm});
            skLineSegment(sketch, "E209.0", {"start": v(-68, -16) * mm, "end": v(-64, -16) * mm});
            skLineSegment(sketch, "E210.0", {"start": v(-68, -16) * mm, "end": v(-68, -24) * mm});
            skLineSegment(sketch, "E211.0", {"start": v(-64, -24) * mm, "end": v(-64, -16) * mm});
            skLineSegment(sketch, "E212.0", {"start": v(-68, -24) * mm, "end": v(-64, -24) * mm});
            skLineSegment(sketch, "E213.0", {"start": v(-68, -36) * mm, "end": v(-64, -36) * mm});
            skLineSegment(sketch, "E214.0", {"start": v(-68, -36) * mm, "end": v(-68, -44) * mm});
            skLineSegment(sketch, "E215.0", {"start": v(-64, -44) * mm, "end": v(-64, -36) * mm});
            skLineSegment(sketch, "E216.0", {"start": v(-68, -44) * mm, "end": v(-64, -44) * mm});
            skLineSegment(sketch, "E217.0", {"start": v(-68, -56) * mm, "end": v(-64, -56) * mm});
            skLineSegment(sketch, "E218.0", {"start": v(-68, -64) * mm, "end": v(-68, -56) * mm});
            skLineSegment(sketch, "E219.0", {"start": v(-68, -64) * mm, "end": v(-64, -64) * mm});
            skLineSegment(sketch, "E220.0", {"start": v(-64, -64) * mm, "end": v(-64, -56) * mm});
            skLineSegment(sketch, "E221", {"start": v(-21, 86.5) * mm, "end": v(-29, 86.5) * mm});
            skLineSegment(sketch, "E222.0", {"start": v(-50, 72.5) * mm, "end": v(22, 72.5) * mm});
            skLineSegment(sketch, "E223.0", {"start": v(-50, 42.5) * mm, "end": v(-50, 72.5) * mm});
            skLineSegment(sketch, "E224.0", {"start": v(-50, 42.5) * mm, "end": v(22, 42.5) * mm});
            skLineSegment(sketch, "E225.0", {"start": v(22, 42.5) * mm, "end": v(22, 72.5) * mm});
            skLineSegment(sketch, "E226.0", {"start": v(-50, -42.5) * mm, "end": v(22, -42.5) * mm});
            skLineSegment(sketch, "E227.0", {"start": v(-50, -42.5) * mm, "end": v(-50, -72.5) * mm});
            skLineSegment(sketch, "E228.0", {"start": v(-50, -72.5) * mm, "end": v(22, -72.5) * mm});
            skLineSegment(sketch, "E229.0", {"start": v(22, -42.5) * mm, "end": v(22, -72.5) * mm});
            skSolve(sketch);
        }
        {
            var Q0;
            Q0=makeQuery(id+"F3.imprint","IMPRINT",FACE,{"disambiguationData":[TD([[makeQuery(id+"F3.imprint","IMPRINT",EDGE,{"derivedFrom":sQuery(id+"F3.wireOp",EDGE,"E122.0")}),-1.0]])]});
            extrude(context, id + "F4", {"entities" : qUnion([Q0]), "depth" : 4 * mm});
        }
        {
            var Q0;
            Q0=makeQuery(id+"F1.opExtrude","CAP_FACE",FACE,{"disambiguationData":[OSD([sQuery(id+"F0.wireOp",EDGE,"E0.bottom"),sQuery(id+"F0.wireOp",EDGE,"E0.top"),sQuery(id+"F0.wireOp",EDGE,"E0.left"),sQuery(id+"F0.wireOp",EDGE,"E0.right"),sQuery(id+"F0.wireOp",EDGE,"E2.bottom"),sQuery(id+"F0.wireOp",EDGE,"E2.top"),sQuery(id+"F0.wireOp",EDGE,"E2.right"),sQuery(id+"F0.wireOp",EDGE,"E3.MirrorCS"),sQuery(id+"F0.wireOp",EDGE,"E4.MirrorCS"),sQuery(id+"F0.wireOp",EDGE,"E5.MirrorCS"),sQuery(id+"F0.wireOp",EDGE,"E6.1.0.0"),sQuery(id+"F0.wireOp",EDGE,"E6.1.0.1"),sQuery(id+"F0.wireOp",EDGE,"E6.1.0.2"),sQuery(id+"F0.wireOp",EDGE,"E6.1.0.3"),sQuery(id+"F0.wireOp",EDGE,"E6.1.0.4"),sQuery(id+"F0.wireOp",EDGE,"E6.1.0.5"),sQuery(id+"F0.wireOp",EDGE,"E6.2.0.0"),sQuery(id+"F0.wireOp",EDGE,"E6.2.0.1"),sQuery(id+"F0.wireOp",EDGE,"E6.2.0.2"),sQuery(id+"F0.wireOp",EDGE,"E6.2.0.3"),sQuery(id+"F0.wireOp",EDGE,"E6.2.0.4"),sQuery(id+"F0.wireOp",EDGE,"E6.2.0.5"),sQuery(id+"F0.wireOp",EDGE,"E7.MirrorCS"),sQuery(id+"F0.wireOp",EDGE,"E8.MirrorCS"),sQuery(id+"F0.wireOp",EDGE,"E9.MirrorCS"),sQuery(id+"F0.wireOp",EDGE,"E10.MirrorCS"),sQuery(id+"F0.wireOp",EDGE,"E11.MirrorCS"),sQuery(id+"F0.wireOp",EDGE,"E12.MirrorCS"),sQuery(id+"F0.wireOp",EDGE,"E13.MirrorCS"),sQuery(id+"F0.wireOp",EDGE,"E14.MirrorCS"),sQuery(id+"F0.wireOp",EDGE,"E15.MirrorCS"),sQuery(id+"F0.wireOp",EDGE,"E16.MirrorCS"),sQuery(id+"F0.wireOp",EDGE,"E17.MirrorCS"),sQuery(id+"F0.wireOp",EDGE,"E18.MirrorCS"),sQuery(id+"F0.wireOp",EDGE,"E21.top"),sQuery(id+"F0.wireOp",EDGE,"E21.left"),sQuery(id+"F0.wireOp",EDGE,"E21.right"),sQuery(id+"F0.wireOp",EDGE,"E22.MirrorCS"),sQuery(id+"F0.wireOp",EDGE,"E23.MirrorCS"),sQuery(id+"F0.wireOp",EDGE,"E24.MirrorCS"),sQuery(id+"F0.wireOp",EDGE,"E25.0.1.0"),sQuery(id+"F0.wireOp",EDGE,"E25.0.1.1"),sQuery(id+"F0.wireOp",EDGE,"E25.0.1.2"),sQuery(id+"F0.wireOp",EDGE,"E25.0.1.3"),sQuery(id+"F0.wireOp",EDGE,"E25.0.1.4"),sQuery(id+"F0.wireOp",EDGE,"E25.0.1.5"),sQuery(id+"F0.wireOp",EDGE,"E25.0.2.0"),sQuery(id+"F0.wireOp",EDGE,"E25.0.2.1"),sQuery(id+"F0.wireOp",EDGE,"E25.0.2.2"),sQuery(id+"F0.wireOp",EDGE,"E25.0.2.3"),sQuery(id+"F0.wireOp",EDGE,"E25.0.2.4"),sQuery(id+"F0.wireOp",EDGE,"E25.0.2.5"),sQuery(id+"F0.wireOp",EDGE,"E25.0.3.0"),sQuery(id+"F0.wireOp",EDGE,"E25.0.3.1"),sQuery(id+"F0.wireOp",EDGE,"E25.0.3.2"),sQuery(id+"F0.wireOp",EDGE,"E25.0.3.3"),sQuery(id+"F0.wireOp",EDGE,"E25.0.3.4"),sQuery(id+"F0.wireOp",EDGE,"E25.0.3.5"),sQuery(id+"F0.wireOp",EDGE,"E26.MirrorCS"),sQuery(id+"F0.wireOp",EDGE,"E27.MirrorCS"),sQuery(id+"F0.wireOp",EDGE,"E28.MirrorCS"),sQuery(id+"F0.wireOp",EDGE,"E29.MirrorCS"),sQuery(id+"F0.wireOp",EDGE,"E30.MirrorCS"),sQuery(id+"F0.wireOp",EDGE,"E31.MirrorCS"),sQuery(id+"F0.wireOp",EDGE,"E32.MirrorCS"),sQuery(id+"F0.wireOp",EDGE,"E33.MirrorCS"),sQuery(id+"F0.wireOp",EDGE,"E34.MirrorCS"),sQuery(id+"F0.wireOp",EDGE,"E35.MirrorCS"),sQuery(id+"F0.wireOp",EDGE,"E36.MirrorCS"),sQuery(id+"F0.wireOp",EDGE,"E37.MirrorCS"),sQuery(id+"F0.wireOp",EDGE,"E38.MirrorCS"),sQuery(id+"F0.wireOp",EDGE,"E39.MirrorCS"),sQuery(id+"F0.wireOp",EDGE,"E40.MirrorCS"),sQuery(id+"F0.wireOp",EDGE,"E41.MirrorCS"),sQuery(id+"F0.wireOp",EDGE,"E42"),sQuery(id+"F0.wireOp",EDGE,"E43.MirrorCS"),sQuery(id+"F0.wireOp",EDGE,"E44.MirrorCS"),sQuery(id+"F0.wireOp",EDGE,"E45.MirrorCS"),sQuery(id+"F0.wireOp",EDGE,"E46.MirrorCS"),sQuery(id+"F0.wireOp",EDGE,"E47.MirrorCS"),sQuery(id+"F0.wireOp",EDGE,"E48.MirrorCS"),sQuery(id+"F0.wireOp",EDGE,"E49.MirrorCS"),sQuery(id+"F0.wireOp",EDGE,"E50.MirrorCS"),sQuery(id+"F0.wireOp",EDGE,"E51.MirrorCS"),sQuery(id+"F0.wireOp",EDGE,"E52.MirrorCS"),sQuery(id+"F0.wireOp",EDGE,"E53.MirrorCS"),sQuery(id+"F0.wireOp",EDGE,"E54.MirrorCS"),sQuery(id+"F0.wireOp",EDGE,"E55.MirrorCS"),sQuery(id+"F0.wireOp",EDGE,"E56.MirrorCS"),sQuery(id+"F0.wireOp",EDGE,"E57.MirrorCS"),sQuery(id+"F0.wireOp",EDGE,"E58.MirrorCS"),sQuery(id+"F0.wireOp",EDGE,"E59.MirrorCS"),sQuery(id+"F0.wireOp",EDGE,"E60.MirrorCS"),sQuery(id+"F0.wireOp",EDGE,"E61.MirrorCS"),sQuery(id+"F0.wireOp",EDGE,"E62.MirrorCS"),sQuery(id+"F0.wireOp",EDGE,"E63.MirrorCS"),sQuery(id+"F0.wireOp",EDGE,"E64.MirrorCS"),sQuery(id+"F0.wireOp",EDGE,"E65.MirrorCS"),sQuery(id+"F0.wireOp",EDGE,"E66.MirrorCS"),sQuery(id+"F0.wireOp",EDGE,"E67.MirrorCS"),sQuery(id+"F0.wireOp",EDGE,"E68.MirrorCS"),sQuery(id+"F0.wireOp",EDGE,"E69.MirrorCS"),sQuery(id+"F0.wireOp",EDGE,"E70.MirrorCS"),sQuery(id+"F0.wireOp",EDGE,"E71.MirrorCS"),sQuery(id+"F0.wireOp",EDGE,"E72.MirrorCS"),sQuery(id+"F0.wireOp",EDGE,"E73.MirrorCS"),sQuery(id+"F0.wireOp",EDGE,"E74.MirrorCS"),sQuery(id+"F0.wireOp",EDGE,"E75.MirrorCS"),sQuery(id+"F0.wireOp",EDGE,"E76.MirrorCS"),sQuery(id+"F0.wireOp",EDGE,"E77.MirrorCS"),sQuery(id+"F0.wireOp",EDGE,"E78.MirrorCS"),sQuery(id+"F0.wireOp",EDGE,"E79.MirrorCS"),sQuery(id+"F0.wireOp",EDGE,"E80.MirrorCS"),sQuery(id+"F0.wireOp",EDGE,"E81"),sQuery(id+"F0.wireOp",EDGE,"E82"),sQuery(id+"F0.wireOp",EDGE,"E83.MirrorCS"),sQuery(id+"F0.wireOp",EDGE,"E84.MirrorCS"),sQuery(id+"F0.wireOp",EDGE,"E85.MirrorCS"),sQuery(id+"F0.wireOp",EDGE,"E86.MirrorCS"),sQuery(id+"F0.wireOp",EDGE,"E87.MirrorCS"),sQuery(id+"F0.wireOp",EDGE,"E88.MirrorCS"),sQuery(id+"F0.wireOp",EDGE,"E89.MirrorCS"),sQuery(id+"F0.wireOp",EDGE,"E90.MirrorCS"),sQuery(id+"F0.wireOp",EDGE,"E91.MirrorCS"),sQuery(id+"F0.wireOp",EDGE,"E92.MirrorCS"),sQuery(id+"F0.wireOp",EDGE,"E93.MirrorCS"),sQuery(id+"F0.wireOp",EDGE,"E94.MirrorCS"),sQuery(id+"F0.wireOp",EDGE,"E95.MirrorCS"),sQuery(id+"F0.wireOp",EDGE,"E96.MirrorCS"),sQuery(id+"F0.wireOp",EDGE,"E97.MirrorCS"),sQuery(id+"F0.wireOp",EDGE,"E98.MirrorCS"),sQuery(id+"F0.wireOp",EDGE,"E99.MirrorCS"),sQuery(id+"F0.wireOp",EDGE,"E100.MirrorCS"),sQuery(id+"F0.wireOp",EDGE,"E101.MirrorCS"),sQuery(id+"F0.wireOp",EDGE,"E102.MirrorCS"),sQuery(id+"F0.wireOp",EDGE,"E103.MirrorCS"),sQuery(id+"F0.wireOp",EDGE,"E104.MirrorCS"),sQuery(id+"F0.wireOp",EDGE,"E105.MirrorCS"),sQuery(id+"F0.wireOp",EDGE,"E106.MirrorCS"),sQuery(id+"F0.wireOp",EDGE,"E107.MirrorCS"),sQuery(id+"F0.wireOp",EDGE,"E108.MirrorCS"),sQuery(id+"F0.wireOp",EDGE,"E109.MirrorCS"),sQuery(id+"F0.wireOp",EDGE,"E110.MirrorCS"),sQuery(id+"F0.wireOp",EDGE,"E111"),sQuery(id+"F0.wireOp",EDGE,"E112"),sQuery(id+"F0.wireOp",EDGE,"E113"),sQuery(id+"F0.wireOp",EDGE,"E114"),sQuery(id+"F0.wireOp",EDGE,"E115"),sQuery(id+"F0.wireOp",EDGE,"E117.MirrorCS"),sQuery(id+"F0.wireOp",EDGE,"E118.MirrorCS"),sQuery(id+"F0.wireOp",EDGE,"E119.MirrorCS"),sQuery(id+"F0.wireOp",EDGE,"E120.MirrorCS")])],"isStart":false});
            var sketch = newSketch(context, id + "F5", { "sketchPlane" : qUnion([Q0])});
            skLineSegment(sketch, "E230.0.0", {"start": v(70, -92.5) * mm, "end": v(70, 92.5) * mm});
            skLineSegment(sketch, "E230.0.1", {"start": v(70, 92.5) * mm, "end": v(-70, 92.5) * mm});
            skLineSegment(sketch, "E230.0.2", {"start": v(-70, 92.5) * mm, "end": v(-70, -92.5) * mm});
            skLineSegment(sketch, "E230.0.3", {"start": v(-70, -92.5) * mm, "end": v(70, -92.5) * mm});
            skLineSegment(sketch, "E231.0", {"start": v(-68, 64) * mm, "end": v(-68, 56) * mm});
            skLineSegment(sketch, "E232.0", {"start": v(-64, 56) * mm, "end": v(-64, 64) * mm});
            skLineSegment(sketch, "E233.0", {"start": v(-68, 64) * mm, "end": v(-64, 64) * mm});
            skLineSegment(sketch, "E234.0", {"start": v(-68, 56) * mm, "end": v(-64, 56) * mm});
            skLineSegment(sketch, "E235", {"start": v(-64, 92.5) * mm, "end": v(-64, -92.5) * mm});
            skLineSegment(sketch, "E236", {"start": v(-68, 92.5) * mm, "end": v(-68, -92.5) * mm});
            skLineSegment(sketch, "E237.0", {"start": v(-54, 86.5) * mm, "end": v(-46, 86.5) * mm});
            skLineSegment(sketch, "E238.0", {"start": v(-46, 90.5) * mm, "end": v(-46, 86.5) * mm});
            skLineSegment(sketch, "E239.0", {"start": v(-54, 90.5) * mm, "end": v(-54, 86.5) * mm});
            skLineSegment(sketch, "E240.0", {"start": v(-54, 90.5) * mm, "end": v(-46, 90.5) * mm});
            skLineSegment(sketch, "E241.0", {"start": v(68, 64) * mm, "end": v(64, 64) * mm});
            skLineSegment(sketch, "E242", {"start": v(64, 92.5) * mm, "end": v(64, -92.5) * mm});
            skLineSegment(sketch, "E243", {"start": v(68, 92.5) * mm, "end": v(68, -92.5) * mm});
            skLineSegment(sketch, "E244", {"start": v(-64, 90.5) * mm, "end": v(64, 90.5) * mm});
            skLineSegment(sketch, "E245", {"start": v(-64, 86.5) * mm, "end": v(64, 86.5) * mm});
            skPoint(sketch, "E245.endSnap0", {"position": v(50, 86.5) * mm});
            skSolve(sketch);
        }
        {
            var Q0;
            {var subQ5=sQuery(id+"F5.wireOp",EDGE,"E241.0");Q0=makeQuery(id+"F5.imprint","IMPRINT",FACE,{"disambiguationData":[TD([[makeQuery(id+"F5.imprint","IMPRINT",EDGE,{"derivedFrom":subQ5}),-1.0]])]});}
            var Q1;
            {var subQ1=makeQuery(id+"F1.opExtrude","CAP_EDGE",EDGE,{"disambiguationData":[OSD([sQuery(id+"F0.wireOp",EDGE,"E48.MirrorCS")])],"isStart":false});Q1=makeQuery(id+"F5.imprint","IMPRINT",FACE,{"disambiguationData":[TD([[makeQuery(id+"F5.imprint","IMPRINT",EDGE,{"derivedFrom":subQ1}),1.0]])]});}
            var Q2;
            {var subQ0=sQuery(id+"F5.wireOp",EDGE,"E241.0");Q2=makeQuery(id+"F5.imprint","IMPRINT",FACE,{"disambiguationData":[TD([[makeQuery(id+"F5.imprint","IMPRINT",EDGE,{"derivedFrom":subQ0}),1.0]])]});}
            var Q3;
            {var subQ1=makeQuery(id+"F1.opExtrude","CAP_EDGE",EDGE,{"disambiguationData":[OSD([sQuery(id+"F0.wireOp",EDGE,"E49.MirrorCS")])],"isStart":false});Q3=makeQuery(id+"F5.imprint","IMPRINT",FACE,{"disambiguationData":[TD([[makeQuery(id+"F5.imprint","IMPRINT",EDGE,{"derivedFrom":subQ1}),1.0]])]});}
            var Q4;
            {var subQ1=makeQuery(id+"F1.opExtrude","CAP_EDGE",EDGE,{"disambiguationData":[OSD([sQuery(id+"F0.wireOp",EDGE,"E52.MirrorCS")])],"isStart":false});Q4=makeQuery(id+"F5.imprint","IMPRINT",FACE,{"disambiguationData":[TD([[makeQuery(id+"F5.imprint","IMPRINT",EDGE,{"derivedFrom":subQ1}),1.0]])]});}
            var Q5;
            {var subQ1=makeQuery(id+"F1.opExtrude","CAP_EDGE",EDGE,{"disambiguationData":[OSD([sQuery(id+"F0.wireOp",EDGE,"E55.MirrorCS")])],"isStart":false});Q5=makeQuery(id+"F5.imprint","IMPRINT",FACE,{"disambiguationData":[TD([[makeQuery(id+"F5.imprint","IMPRINT",EDGE,{"derivedFrom":subQ1}),1.0]])]});}
            var Q6;
            {var subQ1=makeQuery(id+"F1.opExtrude","CAP_EDGE",EDGE,{"disambiguationData":[OSD([sQuery(id+"F0.wireOp",EDGE,"E58.MirrorCS")])],"isStart":false});Q6=makeQuery(id+"F5.imprint","IMPRINT",FACE,{"disambiguationData":[TD([[makeQuery(id+"F5.imprint","IMPRINT",EDGE,{"derivedFrom":subQ1}),1.0]])]});}
            var Q7;
            {var subQ1=makeQuery(id+"F1.opExtrude","CAP_EDGE",EDGE,{"disambiguationData":[OSD([sQuery(id+"F0.wireOp",EDGE,"E61.MirrorCS")])],"isStart":false});Q7=makeQuery(id+"F5.imprint","IMPRINT",FACE,{"disambiguationData":[TD([[makeQuery(id+"F5.imprint","IMPRINT",EDGE,{"derivedFrom":subQ1}),-1.0]])]});}
            var Q8;
            {var subQ1=makeQuery(id+"F1.opExtrude","CAP_EDGE",EDGE,{"disambiguationData":[OSD([sQuery(id+"F0.wireOp",EDGE,"E61.MirrorCS")])],"isStart":false});Q8=makeQuery(id+"F5.imprint","IMPRINT",FACE,{"disambiguationData":[TD([[makeQuery(id+"F5.imprint","IMPRINT",EDGE,{"derivedFrom":subQ1}),1.0]])]});}
            var Q9;
            {var subQ1=makeQuery(id+"F1.opExtrude","CAP_EDGE",EDGE,{"disambiguationData":[OSD([sQuery(id+"F0.wireOp",EDGE,"E64.MirrorCS")])],"isStart":false});Q9=makeQuery(id+"F5.imprint","IMPRINT",FACE,{"disambiguationData":[TD([[makeQuery(id+"F5.imprint","IMPRINT",EDGE,{"derivedFrom":subQ1}),1.0]])]});}
            var Q10;
            {var subQ1=makeQuery(id+"F1.opExtrude","CAP_EDGE",EDGE,{"disambiguationData":[OSD([sQuery(id+"F0.wireOp",EDGE,"E68.MirrorCS")])],"isStart":false});Q10=makeQuery(id+"F5.imprint","IMPRINT",FACE,{"disambiguationData":[TD([[makeQuery(id+"F5.imprint","IMPRINT",EDGE,{"derivedFrom":subQ1}),1.0]])]});}
            var Q11;
            {var subQ1=makeQuery(id+"F1.opExtrude","CAP_EDGE",EDGE,{"disambiguationData":[OSD([sQuery(id+"F0.wireOp",EDGE,"E69.MirrorCS")])],"isStart":false});Q11=makeQuery(id+"F5.imprint","IMPRINT",FACE,{"disambiguationData":[TD([[makeQuery(id+"F5.imprint","IMPRINT",EDGE,{"derivedFrom":subQ1}),1.0]])]});}
            var Q12;
            {var subQ1=makeQuery(id+"F1.opExtrude","CAP_EDGE",EDGE,{"disambiguationData":[OSD([sQuery(id+"F0.wireOp",EDGE,"E74.MirrorCS")])],"isStart":false});Q12=makeQuery(id+"F5.imprint","IMPRINT",FACE,{"disambiguationData":[TD([[makeQuery(id+"F5.imprint","IMPRINT",EDGE,{"derivedFrom":subQ1}),1.0]])]});}
            var Q13;
            {var subQ1=makeQuery(id+"F1.opExtrude","CAP_EDGE",EDGE,{"disambiguationData":[OSD([sQuery(id+"F0.wireOp",EDGE,"E75.MirrorCS")])],"isStart":false});Q13=makeQuery(id+"F5.imprint","IMPRINT",FACE,{"disambiguationData":[TD([[makeQuery(id+"F5.imprint","IMPRINT",EDGE,{"derivedFrom":subQ1}),1.0]])]});}
            var Q14;
            {var subQ5=makeQuery(id+"F1.opExtrude","CAP_EDGE",EDGE,{"disambiguationData":[OSD([sQuery(id+"F0.wireOp",EDGE,"E79.MirrorCS")])],"isStart":false});Q14=makeQuery(id+"F5.imprint","IMPRINT",FACE,{"disambiguationData":[TD([[makeQuery(id+"F5.imprint","IMPRINT",EDGE,{"derivedFrom":subQ5}),1.0]])]});}
            extrude(context, id + "F6", {"entities" : qUnion([Q0, Q1, Q2, Q3, Q4, Q5, Q6, Q7, Q8, Q9, Q10, Q11, Q12, Q13, Q14]), "depth" : 35 * mm});
        }
        {
            var Q0;
            Q0=makeQuery(id+"F1.opExtrude","CAP_FACE",FACE,{"disambiguationData":[OSD([sQuery(id+"F0.wireOp",EDGE,"E0.bottom"),sQuery(id+"F0.wireOp",EDGE,"E0.top"),sQuery(id+"F0.wireOp",EDGE,"E0.left"),sQuery(id+"F0.wireOp",EDGE,"E0.right"),sQuery(id+"F0.wireOp",EDGE,"E2.bottom"),sQuery(id+"F0.wireOp",EDGE,"E2.top"),sQuery(id+"F0.wireOp",EDGE,"E2.right"),sQuery(id+"F0.wireOp",EDGE,"E3.MirrorCS"),sQuery(id+"F0.wireOp",EDGE,"E4.MirrorCS"),sQuery(id+"F0.wireOp",EDGE,"E5.MirrorCS"),sQuery(id+"F0.wireOp",EDGE,"E6.1.0.0"),sQuery(id+"F0.wireOp",EDGE,"E6.1.0.1"),sQuery(id+"F0.wireOp",EDGE,"E6.1.0.2"),sQuery(id+"F0.wireOp",EDGE,"E6.1.0.3"),sQuery(id+"F0.wireOp",EDGE,"E6.1.0.4"),sQuery(id+"F0.wireOp",EDGE,"E6.1.0.5"),sQuery(id+"F0.wireOp",EDGE,"E6.2.0.0"),sQuery(id+"F0.wireOp",EDGE,"E6.2.0.1"),sQuery(id+"F0.wireOp",EDGE,"E6.2.0.2"),sQuery(id+"F0.wireOp",EDGE,"E6.2.0.3"),sQuery(id+"F0.wireOp",EDGE,"E6.2.0.4"),sQuery(id+"F0.wireOp",EDGE,"E6.2.0.5"),sQuery(id+"F0.wireOp",EDGE,"E7.MirrorCS"),sQuery(id+"F0.wireOp",EDGE,"E8.MirrorCS"),sQuery(id+"F0.wireOp",EDGE,"E9.MirrorCS"),sQuery(id+"F0.wireOp",EDGE,"E10.MirrorCS"),sQuery(id+"F0.wireOp",EDGE,"E11.MirrorCS"),sQuery(id+"F0.wireOp",EDGE,"E12.MirrorCS"),sQuery(id+"F0.wireOp",EDGE,"E13.MirrorCS"),sQuery(id+"F0.wireOp",EDGE,"E14.MirrorCS"),sQuery(id+"F0.wireOp",EDGE,"E15.MirrorCS"),sQuery(id+"F0.wireOp",EDGE,"E16.MirrorCS"),sQuery(id+"F0.wireOp",EDGE,"E17.MirrorCS"),sQuery(id+"F0.wireOp",EDGE,"E18.MirrorCS"),sQuery(id+"F0.wireOp",EDGE,"E21.top"),sQuery(id+"F0.wireOp",EDGE,"E21.left"),sQuery(id+"F0.wireOp",EDGE,"E21.right"),sQuery(id+"F0.wireOp",EDGE,"E22.MirrorCS"),sQuery(id+"F0.wireOp",EDGE,"E23.MirrorCS"),sQuery(id+"F0.wireOp",EDGE,"E24.MirrorCS"),sQuery(id+"F0.wireOp",EDGE,"E25.0.1.0"),sQuery(id+"F0.wireOp",EDGE,"E25.0.1.1"),sQuery(id+"F0.wireOp",EDGE,"E25.0.1.2"),sQuery(id+"F0.wireOp",EDGE,"E25.0.1.3"),sQuery(id+"F0.wireOp",EDGE,"E25.0.1.4"),sQuery(id+"F0.wireOp",EDGE,"E25.0.1.5"),sQuery(id+"F0.wireOp",EDGE,"E25.0.2.0"),sQuery(id+"F0.wireOp",EDGE,"E25.0.2.1"),sQuery(id+"F0.wireOp",EDGE,"E25.0.2.2"),sQuery(id+"F0.wireOp",EDGE,"E25.0.2.3"),sQuery(id+"F0.wireOp",EDGE,"E25.0.2.4"),sQuery(id+"F0.wireOp",EDGE,"E25.0.2.5"),sQuery(id+"F0.wireOp",EDGE,"E25.0.3.0"),sQuery(id+"F0.wireOp",EDGE,"E25.0.3.1"),sQuery(id+"F0.wireOp",EDGE,"E25.0.3.2"),sQuery(id+"F0.wireOp",EDGE,"E25.0.3.3"),sQuery(id+"F0.wireOp",EDGE,"E25.0.3.4"),sQuery(id+"F0.wireOp",EDGE,"E25.0.3.5"),sQuery(id+"F0.wireOp",EDGE,"E26.MirrorCS"),sQuery(id+"F0.wireOp",EDGE,"E27.MirrorCS"),sQuery(id+"F0.wireOp",EDGE,"E28.MirrorCS"),sQuery(id+"F0.wireOp",EDGE,"E29.MirrorCS"),sQuery(id+"F0.wireOp",EDGE,"E30.MirrorCS"),sQuery(id+"F0.wireOp",EDGE,"E31.MirrorCS"),sQuery(id+"F0.wireOp",EDGE,"E32.MirrorCS"),sQuery(id+"F0.wireOp",EDGE,"E33.MirrorCS"),sQuery(id+"F0.wireOp",EDGE,"E34.MirrorCS"),sQuery(id+"F0.wireOp",EDGE,"E35.MirrorCS"),sQuery(id+"F0.wireOp",EDGE,"E36.MirrorCS"),sQuery(id+"F0.wireOp",EDGE,"E37.MirrorCS"),sQuery(id+"F0.wireOp",EDGE,"E38.MirrorCS"),sQuery(id+"F0.wireOp",EDGE,"E39.MirrorCS"),sQuery(id+"F0.wireOp",EDGE,"E40.MirrorCS"),sQuery(id+"F0.wireOp",EDGE,"E41.MirrorCS"),sQuery(id+"F0.wireOp",EDGE,"E42"),sQuery(id+"F0.wireOp",EDGE,"E43.MirrorCS"),sQuery(id+"F0.wireOp",EDGE,"E44.MirrorCS"),sQuery(id+"F0.wireOp",EDGE,"E45.MirrorCS"),sQuery(id+"F0.wireOp",EDGE,"E46.MirrorCS"),sQuery(id+"F0.wireOp",EDGE,"E47.MirrorCS"),sQuery(id+"F0.wireOp",EDGE,"E48.MirrorCS"),sQuery(id+"F0.wireOp",EDGE,"E49.MirrorCS"),sQuery(id+"F0.wireOp",EDGE,"E50.MirrorCS"),sQuery(id+"F0.wireOp",EDGE,"E51.MirrorCS"),sQuery(id+"F0.wireOp",EDGE,"E52.MirrorCS"),sQuery(id+"F0.wireOp",EDGE,"E53.MirrorCS"),sQuery(id+"F0.wireOp",EDGE,"E54.MirrorCS"),sQuery(id+"F0.wireOp",EDGE,"E55.MirrorCS"),sQuery(id+"F0.wireOp",EDGE,"E56.MirrorCS"),sQuery(id+"F0.wireOp",EDGE,"E57.MirrorCS"),sQuery(id+"F0.wireOp",EDGE,"E58.MirrorCS"),sQuery(id+"F0.wireOp",EDGE,"E59.MirrorCS"),sQuery(id+"F0.wireOp",EDGE,"E60.MirrorCS"),sQuery(id+"F0.wireOp",EDGE,"E61.MirrorCS"),sQuery(id+"F0.wireOp",EDGE,"E62.MirrorCS"),sQuery(id+"F0.wireOp",EDGE,"E63.MirrorCS"),sQuery(id+"F0.wireOp",EDGE,"E64.MirrorCS"),sQuery(id+"F0.wireOp",EDGE,"E65.MirrorCS"),sQuery(id+"F0.wireOp",EDGE,"E66.MirrorCS"),sQuery(id+"F0.wireOp",EDGE,"E67.MirrorCS"),sQuery(id+"F0.wireOp",EDGE,"E68.MirrorCS"),sQuery(id+"F0.wireOp",EDGE,"E69.MirrorCS"),sQuery(id+"F0.wireOp",EDGE,"E70.MirrorCS"),sQuery(id+"F0.wireOp",EDGE,"E71.MirrorCS"),sQuery(id+"F0.wireOp",EDGE,"E72.MirrorCS"),sQuery(id+"F0.wireOp",EDGE,"E73.MirrorCS"),sQuery(id+"F0.wireOp",EDGE,"E74.MirrorCS"),sQuery(id+"F0.wireOp",EDGE,"E75.MirrorCS"),sQuery(id+"F0.wireOp",EDGE,"E76.MirrorCS"),sQuery(id+"F0.wireOp",EDGE,"E77.MirrorCS"),sQuery(id+"F0.wireOp",EDGE,"E78.MirrorCS"),sQuery(id+"F0.wireOp",EDGE,"E79.MirrorCS"),sQuery(id+"F0.wireOp",EDGE,"E80.MirrorCS"),sQuery(id+"F0.wireOp",EDGE,"E81"),sQuery(id+"F0.wireOp",EDGE,"E82"),sQuery(id+"F0.wireOp",EDGE,"E83.MirrorCS"),sQuery(id+"F0.wireOp",EDGE,"E84.MirrorCS"),sQuery(id+"F0.wireOp",EDGE,"E85.MirrorCS"),sQuery(id+"F0.wireOp",EDGE,"E86.MirrorCS"),sQuery(id+"F0.wireOp",EDGE,"E87.MirrorCS"),sQuery(id+"F0.wireOp",EDGE,"E88.MirrorCS"),sQuery(id+"F0.wireOp",EDGE,"E89.MirrorCS"),sQuery(id+"F0.wireOp",EDGE,"E90.MirrorCS"),sQuery(id+"F0.wireOp",EDGE,"E91.MirrorCS"),sQuery(id+"F0.wireOp",EDGE,"E92.MirrorCS"),sQuery(id+"F0.wireOp",EDGE,"E93.MirrorCS"),sQuery(id+"F0.wireOp",EDGE,"E94.MirrorCS"),sQuery(id+"F0.wireOp",EDGE,"E95.MirrorCS"),sQuery(id+"F0.wireOp",EDGE,"E96.MirrorCS"),sQuery(id+"F0.wireOp",EDGE,"E97.MirrorCS"),sQuery(id+"F0.wireOp",EDGE,"E98.MirrorCS"),sQuery(id+"F0.wireOp",EDGE,"E99.MirrorCS"),sQuery(id+"F0.wireOp",EDGE,"E100.MirrorCS"),sQuery(id+"F0.wireOp",EDGE,"E101.MirrorCS"),sQuery(id+"F0.wireOp",EDGE,"E102.MirrorCS"),sQuery(id+"F0.wireOp",EDGE,"E103.MirrorCS"),sQuery(id+"F0.wireOp",EDGE,"E104.MirrorCS"),sQuery(id+"F0.wireOp",EDGE,"E105.MirrorCS"),sQuery(id+"F0.wireOp",EDGE,"E106.MirrorCS"),sQuery(id+"F0.wireOp",EDGE,"E107.MirrorCS"),sQuery(id+"F0.wireOp",EDGE,"E108.MirrorCS"),sQuery(id+"F0.wireOp",EDGE,"E109.MirrorCS"),sQuery(id+"F0.wireOp",EDGE,"E110.MirrorCS"),sQuery(id+"F0.wireOp",EDGE,"E111"),sQuery(id+"F0.wireOp",EDGE,"E112"),sQuery(id+"F0.wireOp",EDGE,"E113"),sQuery(id+"F0.wireOp",EDGE,"E114"),sQuery(id+"F0.wireOp",EDGE,"E115"),sQuery(id+"F0.wireOp",EDGE,"E117.MirrorCS"),sQuery(id+"F0.wireOp",EDGE,"E118.MirrorCS"),sQuery(id+"F0.wireOp",EDGE,"E119.MirrorCS"),sQuery(id+"F0.wireOp",EDGE,"E120.MirrorCS")])],"isStart":false});
            var sketch = newSketch(context, id + "F7", { "sketchPlane" : qUnion([Q0])});
            skLineSegment(sketch, "E246.0", {"start": v(46, -90.5) * mm, "end": v(46, -86.5) * mm});
            skLineSegment(sketch, "E247.0", {"start": v(54, -86.5) * mm, "end": v(46, -86.5) * mm});
            skLineSegment(sketch, "E248.0", {"start": v(54, -90.5) * mm, "end": v(46, -90.5) * mm});
            skLineSegment(sketch, "E249.0", {"start": v(54, -90.5) * mm, "end": v(54, -86.5) * mm});
            skLineSegment(sketch, "E250.0", {"start": v(21, -90.5) * mm, "end": v(21, -86.5) * mm});
            skLineSegment(sketch, "E251.0", {"start": v(29, -90.5) * mm, "end": v(21, -90.5) * mm});
            skLineSegment(sketch, "E252.0", {"start": v(29, -86.5) * mm, "end": v(21, -86.5) * mm});
            skLineSegment(sketch, "E253.0", {"start": v(29, -90.5) * mm, "end": v(29, -86.5) * mm});
            skLineSegment(sketch, "E254.0", {"start": v(-4, -90.5) * mm, "end": v(-4, -86.5) * mm});
            skLineSegment(sketch, "E255.0", {"start": v(-4, -90.5) * mm, "end": v(4, -90.5) * mm});
            skLineSegment(sketch, "E256.0", {"start": v(-4, -86.5) * mm, "end": v(4, -86.5) * mm});
            skLineSegment(sketch, "E257.0", {"start": v(4, -90.5) * mm, "end": v(4, -86.5) * mm});
            skLineSegment(sketch, "E258.0", {"start": v(-29, -90.5) * mm, "end": v(-29, -86.5) * mm});
            skLineSegment(sketch, "E259.0", {"start": v(-21, -90.5) * mm, "end": v(-29, -90.5) * mm});
            skLineSegment(sketch, "E260.0", {"start": v(-21, -90.5) * mm, "end": v(-21, -86.5) * mm});
            skLineSegment(sketch, "E261.0", {"start": v(-21, -86.5) * mm, "end": v(-29, -86.5) * mm});
            skLineSegment(sketch, "E262.0", {"start": v(-54, -90.5) * mm, "end": v(-54, -86.5) * mm});
            skLineSegment(sketch, "E263.0", {"start": v(-46, -90.5) * mm, "end": v(-54, -90.5) * mm});
            skLineSegment(sketch, "E264.0", {"start": v(-46, -90.5) * mm, "end": v(-46, -86.5) * mm});
            skLineSegment(sketch, "E265.0", {"start": v(-46, -86.5) * mm, "end": v(-54, -86.5) * mm});
            skLineSegment(sketch, "E266.0", {"start": v(64, -56) * mm, "end": v(64, -64) * mm});
            skLineSegment(sketch, "E267.0", {"start": v(68, -64) * mm, "end": v(64, -64) * mm});
            skLineSegment(sketch, "E268.0", {"start": v(68, -64) * mm, "end": v(68, -56) * mm});
            skLineSegment(sketch, "E269.0", {"start": v(68, -56) * mm, "end": v(64, -56) * mm});
            skLineSegment(sketch, "E270.0", {"start": v(64, -36) * mm, "end": v(64, -44) * mm});
            skLineSegment(sketch, "E271.0", {"start": v(68, -44) * mm, "end": v(64, -44) * mm});
            skLineSegment(sketch, "E272.0", {"start": v(68, -36) * mm, "end": v(68, -44) * mm});
            skLineSegment(sketch, "E273.0", {"start": v(68, -36) * mm, "end": v(64, -36) * mm});
            skLineSegment(sketch, "E274.0", {"start": v(64, -16) * mm, "end": v(64, -24) * mm});
            skLineSegment(sketch, "E275.0", {"start": v(68, -24) * mm, "end": v(64, -24) * mm});
            skLineSegment(sketch, "E276.0", {"start": v(68, -16) * mm, "end": v(68, -24) * mm});
            skLineSegment(sketch, "E277.0", {"start": v(68, -16) * mm, "end": v(64, -16) * mm});
            skLineSegment(sketch, "E278.0", {"start": v(64, -4) * mm, "end": v(64, 4) * mm});
            skLineSegment(sketch, "E279.0", {"start": v(68, -4) * mm, "end": v(64, -4) * mm});
            skLineSegment(sketch, "E280.0", {"start": v(68, -4) * mm, "end": v(68, 4) * mm});
            skLineSegment(sketch, "E281.0", {"start": v(64, 4) * mm, "end": v(68, 4) * mm});
            skLineSegment(sketch, "E282.0", {"start": v(64, 24) * mm, "end": v(64, 16) * mm});
            skPoint(sketch, "E283.0", {"position": v(66, 16) * mm});
            skPoint(sketch, "E284.0", {"position": v(68, 20) * mm});
            skLineSegment(sketch, "E285.0", {"start": v(68, 24) * mm, "end": v(68, 16) * mm});
            skLineSegment(sketch, "E286.0", {"start": v(68, 16) * mm, "end": v(64, 16) * mm});
            skLineSegment(sketch, "E287.0", {"start": v(68, 24) * mm, "end": v(64, 24) * mm});
            skLineSegment(sketch, "E288.0", {"start": v(64, 44) * mm, "end": v(64, 36) * mm});
            skLineSegment(sketch, "E289.0", {"start": v(68, 36) * mm, "end": v(64, 36) * mm});
            skLineSegment(sketch, "E290.0", {"start": v(68, 36) * mm, "end": v(68, 44) * mm});
            skLineSegment(sketch, "E291.0", {"start": v(68, 44) * mm, "end": v(64, 44) * mm});
            skLineSegment(sketch, "E292.0", {"start": v(64, 64) * mm, "end": v(64, 56) * mm});
            skLineSegment(sketch, "E293.0", {"start": v(68, 56) * mm, "end": v(64, 56) * mm});
            skLineSegment(sketch, "E294.0", {"start": v(68, 64) * mm, "end": v(68, 56) * mm});
            skLineSegment(sketch, "E295.0", {"start": v(68, 64) * mm, "end": v(64, 64) * mm});
            skLineSegment(sketch, "E296.0", {"start": v(-54, 90.5) * mm, "end": v(-54, 86.5) * mm});
            skLineSegment(sketch, "E297.0", {"start": v(-54, 86.5) * mm, "end": v(-46, 86.5) * mm});
            skLineSegment(sketch, "E298.0", {"start": v(-54, 90.5) * mm, "end": v(-46, 90.5) * mm});
            skLineSegment(sketch, "E299.0", {"start": v(-46, 90.5) * mm, "end": v(-46, 86.5) * mm});
            skLineSegment(sketch, "E300.0", {"start": v(-29, 90.5) * mm, "end": v(-29, 86.5) * mm});
            skLineSegment(sketch, "E301.0", {"start": v(-21, 86.5) * mm, "end": v(-29, 86.5) * mm});
            skLineSegment(sketch, "E302.0", {"start": v(-21, 90.5) * mm, "end": v(-29, 90.5) * mm});
            skLineSegment(sketch, "E303.0", {"start": v(-4, 90.5) * mm, "end": v(-4, 86.5) * mm});
            skLineSegment(sketch, "E304.0", {"start": v(-4, 86.5) * mm, "end": v(4, 86.5) * mm});
            skLineSegment(sketch, "E305.0", {"start": v(4, 90.5) * mm, "end": v(4, 86.5) * mm});
            skLineSegment(sketch, "E306.0", {"start": v(4, 90.5) * mm, "end": v(-4, 90.5) * mm});
            skLineSegment(sketch, "E307.0", {"start": v(21, 90.5) * mm, "end": v(21, 86.5) * mm});
            skLineSegment(sketch, "E308.0", {"start": v(21, 86.5) * mm, "end": v(29, 86.5) * mm});
            skLineSegment(sketch, "E309.0", {"start": v(29, 90.5) * mm, "end": v(29, 86.5) * mm});
            skLineSegment(sketch, "E310.0", {"start": v(21, 90.5) * mm, "end": v(29, 90.5) * mm});
            skLineSegment(sketch, "E311.0", {"start": v(46, 90.5) * mm, "end": v(46, 86.5) * mm});
            skLineSegment(sketch, "E312.0", {"start": v(46, 86.5) * mm, "end": v(54, 86.5) * mm});
            skLineSegment(sketch, "E313.0", {"start": v(54, 90.5) * mm, "end": v(54, 86.5) * mm});
            skLineSegment(sketch, "E314.0", {"start": v(46, 90.5) * mm, "end": v(54, 90.5) * mm});
            skSolve(sketch);
        }
        {
            var Q0;
            Q0=makeQuery(id+"F4.opExtrude","CAP_FACE",FACE,{"disambiguationData":[OSD([sQuery(id+"F3.wireOp",EDGE,"E122.0"),sQuery(id+"F3.wireOp",EDGE,"E123.0"),sQuery(id+"F3.wireOp",EDGE,"E124.0"),sQuery(id+"F3.wireOp",EDGE,"E125.0"),sQuery(id+"F3.wireOp",EDGE,"E126.0"),sQuery(id+"F3.wireOp",EDGE,"E127.0"),sQuery(id+"F3.wireOp",EDGE,"E128.0"),sQuery(id+"F3.wireOp",EDGE,"E129.0"),sQuery(id+"F3.wireOp",EDGE,"E131.0"),sQuery(id+"F3.wireOp",EDGE,"E132.0"),sQuery(id+"F3.wireOp",EDGE,"E133.0"),sQuery(id+"F3.wireOp",EDGE,"E134.0"),sQuery(id+"F3.wireOp",EDGE,"E135.0"),sQuery(id+"F3.wireOp",EDGE,"E136.0"),sQuery(id+"F3.wireOp",EDGE,"E137.0"),sQuery(id+"F3.wireOp",EDGE,"E138.0"),sQuery(id+"F3.wireOp",EDGE,"E139.0"),sQuery(id+"F3.wireOp",EDGE,"E140.0"),sQuery(id+"F3.wireOp",EDGE,"E141.0"),sQuery(id+"F3.wireOp",EDGE,"E142.0"),sQuery(id+"F3.wireOp",EDGE,"E143.0.0"),sQuery(id+"F3.wireOp",EDGE,"E143.0.1"),sQuery(id+"F3.wireOp",EDGE,"E143.0.2"),sQuery(id+"F3.wireOp",EDGE,"E143.0.3"),sQuery(id+"F3.wireOp",EDGE,"E144.0"),sQuery(id+"F3.wireOp",EDGE,"E145.0"),sQuery(id+"F3.wireOp",EDGE,"E146.0"),sQuery(id+"F3.wireOp",EDGE,"E147.0"),sQuery(id+"F3.wireOp",EDGE,"E148.0"),sQuery(id+"F3.wireOp",EDGE,"E149.0"),sQuery(id+"F3.wireOp",EDGE,"E150.0"),sQuery(id+"F3.wireOp",EDGE,"E151.0"),sQuery(id+"F3.wireOp",EDGE,"E152.0"),sQuery(id+"F3.wireOp",EDGE,"E153.0.2"),sQuery(id+"F3.wireOp",EDGE,"E154.0"),sQuery(id+"F3.wireOp",EDGE,"E155.0"),sQuery(id+"F3.wireOp",EDGE,"E156.0"),sQuery(id+"F3.wireOp",EDGE,"E157.0.2"),sQuery(id+"F3.wireOp",EDGE,"E158.0"),sQuery(id+"F3.wireOp",EDGE,"E159.0"),sQuery(id+"F3.wireOp",EDGE,"E160.0"),sQuery(id+"F3.wireOp",EDGE,"E161.0"),sQuery(id+"F3.wireOp",EDGE,"E162.0"),sQuery(id+"F3.wireOp",EDGE,"E163.0"),sQuery(id+"F3.wireOp",EDGE,"E164.0"),sQuery(id+"F3.wireOp",EDGE,"E165.0"),sQuery(id+"F3.wireOp",EDGE,"E166.0"),sQuery(id+"F3.wireOp",EDGE,"E167.0"),sQuery(id+"F3.wireOp",EDGE,"E168.0"),sQuery(id+"F3.wireOp",EDGE,"E169.0"),sQuery(id+"F3.wireOp",EDGE,"E170.0"),sQuery(id+"F3.wireOp",EDGE,"E171.0"),sQuery(id+"F3.wireOp",EDGE,"E172.0"),sQuery(id+"F3.wireOp",EDGE,"E173.0"),sQuery(id+"F3.wireOp",EDGE,"E174.0"),sQuery(id+"F3.wireOp",EDGE,"E175.0"),sQuery(id+"F3.wireOp",EDGE,"E176.0"),sQuery(id+"F3.wireOp",EDGE,"E177.0"),sQuery(id+"F3.wireOp",EDGE,"E178.0"),sQuery(id+"F3.wireOp",EDGE,"E179.0"),sQuery(id+"F3.wireOp",EDGE,"E180.0"),sQuery(id+"F3.wireOp",EDGE,"E181.0"),sQuery(id+"F3.wireOp",EDGE,"E182.0"),sQuery(id+"F3.wireOp",EDGE,"E183.0"),sQuery(id+"F3.wireOp",EDGE,"E184.0"),sQuery(id+"F3.wireOp",EDGE,"E187.0"),sQuery(id+"F3.wireOp",EDGE,"E188.0"),sQuery(id+"F3.wireOp",EDGE,"E189.0"),sQuery(id+"F3.wireOp",EDGE,"E190.0"),sQuery(id+"F3.wireOp",EDGE,"E191.0"),sQuery(id+"F3.wireOp",EDGE,"E192.0"),sQuery(id+"F3.wireOp",EDGE,"E193.0"),sQuery(id+"F3.wireOp",EDGE,"E194.0"),sQuery(id+"F3.wireOp",EDGE,"E195.0"),sQuery(id+"F3.wireOp",EDGE,"E196.0"),sQuery(id+"F3.wireOp",EDGE,"E197.0"),sQuery(id+"F3.wireOp",EDGE,"E198.0"),sQuery(id+"F3.wireOp",EDGE,"E199.0"),sQuery(id+"F3.wireOp",EDGE,"E200.0"),sQuery(id+"F3.wireOp",EDGE,"E201.0"),sQuery(id+"F3.wireOp",EDGE,"E202.0"),sQuery(id+"F3.wireOp",EDGE,"E203.0"),sQuery(id+"F3.wireOp",EDGE,"E204.0"),sQuery(id+"F3.wireOp",EDGE,"E205.0"),sQuery(id+"F3.wireOp",EDGE,"E206.0"),sQuery(id+"F3.wireOp",EDGE,"E207.0"),sQuery(id+"F3.wireOp",EDGE,"E208.0"),sQuery(id+"F3.wireOp",EDGE,"E209.0"),sQuery(id+"F3.wireOp",EDGE,"E210.0"),sQuery(id+"F3.wireOp",EDGE,"E211.0"),sQuery(id+"F3.wireOp",EDGE,"E212.0"),sQuery(id+"F3.wireOp",EDGE,"E213.0"),sQuery(id+"F3.wireOp",EDGE,"E214.0"),sQuery(id+"F3.wireOp",EDGE,"E215.0"),sQuery(id+"F3.wireOp",EDGE,"E216.0"),sQuery(id+"F3.wireOp",EDGE,"E217.0"),sQuery(id+"F3.wireOp",EDGE,"E218.0"),sQuery(id+"F3.wireOp",EDGE,"E219.0"),sQuery(id+"F3.wireOp",EDGE,"E220.0"),sQuery(id+"F3.wireOp",EDGE,"E221"),sQuery(id+"F3.wireOp",EDGE,"E222.0"),sQuery(id+"F3.wireOp",EDGE,"E223.0"),sQuery(id+"F3.wireOp",EDGE,"E224.0"),sQuery(id+"F3.wireOp",EDGE,"E225.0"),sQuery(id+"F3.wireOp",EDGE,"E226.0"),sQuery(id+"F3.wireOp",EDGE,"E227.0"),sQuery(id+"F3.wireOp",EDGE,"E228.0"),sQuery(id+"F3.wireOp",EDGE,"E229.0")])],"isStart":false});
            var sketch = newSketch(context, id + "F8", { "sketchPlane" : qUnion([Q0])});
            skLineSegment(sketch, "E315.0", {"start": v(46, -90.5) * mm, "end": v(46, -86.5) * mm});
            skLineSegment(sketch, "E316.0", {"start": v(54, -90.5) * mm, "end": v(46, -90.5) * mm});
            skLineSegment(sketch, "E317.0", {"start": v(54, -90.5) * mm, "end": v(54, -86.5) * mm});
            skLineSegment(sketch, "E318.0", {"start": v(54, -86.5) * mm, "end": v(46, -86.5) * mm});
            skLineSegment(sketch, "E319.0", {"start": v(21, -90.5) * mm, "end": v(21, -86.5) * mm});
            skLineSegment(sketch, "E320.0", {"start": v(29, -90.5) * mm, "end": v(21, -90.5) * mm});
            skLineSegment(sketch, "E321.0", {"start": v(29, -90.5) * mm, "end": v(29, -86.5) * mm});
            skLineSegment(sketch, "E322.0", {"start": v(29, -86.5) * mm, "end": v(21, -86.5) * mm});
            skLineSegment(sketch, "E323.0", {"start": v(-4, -90.5) * mm, "end": v(-4, -86.5) * mm});
            skLineSegment(sketch, "E324.0", {"start": v(-4, -90.5) * mm, "end": v(4, -90.5) * mm});
            skLineSegment(sketch, "E325.0", {"start": v(4, -90.5) * mm, "end": v(4, -86.5) * mm});
            skLineSegment(sketch, "E326.0", {"start": v(-4, -86.5) * mm, "end": v(4, -86.5) * mm});
            skLineSegment(sketch, "E327.0", {"start": v(-29, -90.5) * mm, "end": v(-29, -86.5) * mm});
            skLineSegment(sketch, "E328.0", {"start": v(-21, -90.5) * mm, "end": v(-29, -90.5) * mm});
            skLineSegment(sketch, "E329.0", {"start": v(-21, -90.5) * mm, "end": v(-21, -86.5) * mm});
            skLineSegment(sketch, "E330.0", {"start": v(-21, -86.5) * mm, "end": v(-29, -86.5) * mm});
            skLineSegment(sketch, "E331.0", {"start": v(-54, -90.5) * mm, "end": v(-54, -86.5) * mm});
            skPoint(sketch, "E332.0", {"position": v(-54, -90.5) * mm});
            skLineSegment(sketch, "E333.0", {"start": v(-46, -90.5) * mm, "end": v(-54, -90.5) * mm});
            skLineSegment(sketch, "E334.0", {"start": v(-46, -90.5) * mm, "end": v(-46, -86.5) * mm});
            skLineSegment(sketch, "E335.0", {"start": v(-46, -86.5) * mm, "end": v(-54, -86.5) * mm});
            skLineSegment(sketch, "E336.0", {"start": v(64, -56) * mm, "end": v(64, -64) * mm});
            skLineSegment(sketch, "E337.0", {"start": v(68, -64) * mm, "end": v(64, -64) * mm});
            skLineSegment(sketch, "E338.0", {"start": v(68, -64) * mm, "end": v(68, -56) * mm});
            skLineSegment(sketch, "E339.0", {"start": v(64, -36) * mm, "end": v(64, -44) * mm});
            skLineSegment(sketch, "E340.0", {"start": v(68, -44) * mm, "end": v(64, -44) * mm});
            skLineSegment(sketch, "E341.0", {"start": v(68, -36) * mm, "end": v(68, -44) * mm});
            skLineSegment(sketch, "E342.0", {"start": v(68, -36) * mm, "end": v(64, -36) * mm});
            skLineSegment(sketch, "E343.0", {"start": v(64, -16) * mm, "end": v(64, -24) * mm});
            skLineSegment(sketch, "E344.0", {"start": v(68, -24) * mm, "end": v(64, -24) * mm});
            skLineSegment(sketch, "E345.0", {"start": v(68, -16) * mm, "end": v(68, -24) * mm});
            skLineSegment(sketch, "E346.0", {"start": v(68, -16) * mm, "end": v(64, -16) * mm});
            skLineSegment(sketch, "E347.0", {"start": v(64, 4) * mm, "end": v(64, -4) * mm});
            skLineSegment(sketch, "E348.0", {"start": v(68, -4) * mm, "end": v(64, -4) * mm});
            skLineSegment(sketch, "E349.0", {"start": v(68, -4) * mm, "end": v(68, 4) * mm});
            skLineSegment(sketch, "E350.0", {"start": v(64, 4) * mm, "end": v(68, 4) * mm});
            skLineSegment(sketch, "E351.0", {"start": v(64, 24) * mm, "end": v(64, 16) * mm});
            skLineSegment(sketch, "E352.0", {"start": v(68, 16) * mm, "end": v(64, 16) * mm});
            skLineSegment(sketch, "E353.0", {"start": v(68, 24) * mm, "end": v(68, 16) * mm});
            skLineSegment(sketch, "E354.0", {"start": v(68, 24) * mm, "end": v(64, 24) * mm});
            skLineSegment(sketch, "E355.0", {"start": v(64, 44) * mm, "end": v(64, 36) * mm});
            skLineSegment(sketch, "E356.0", {"start": v(68, 36) * mm, "end": v(64, 36) * mm});
            skLineSegment(sketch, "E357.0", {"start": v(68, 36) * mm, "end": v(68, 44) * mm});
            skLineSegment(sketch, "E358.0", {"start": v(68, 44) * mm, "end": v(64, 44) * mm});
            skLineSegment(sketch, "E359.0", {"start": v(64, 64) * mm, "end": v(64, 56) * mm});
            skLineSegment(sketch, "E360.0", {"start": v(68, 56) * mm, "end": v(64, 56) * mm});
            skLineSegment(sketch, "E361.0", {"start": v(68, 64) * mm, "end": v(68, 56) * mm});
            skLineSegment(sketch, "E362.0", {"start": v(68, 64) * mm, "end": v(64, 64) * mm});
            skLineSegment(sketch, "E363.0", {"start": v(46, 90.5) * mm, "end": v(46, 86.5) * mm});
            skLineSegment(sketch, "E364.0", {"start": v(46, 86.5) * mm, "end": v(54, 86.5) * mm});
            skLineSegment(sketch, "E365.0", {"start": v(46, 90.5) * mm, "end": v(54, 90.5) * mm});
            skLineSegment(sketch, "E366.0", {"start": v(54, 90.5) * mm, "end": v(54, 86.5) * mm});
            skLineSegment(sketch, "E367.0", {"start": v(21, 90.5) * mm, "end": v(21, 86.5) * mm});
            skLineSegment(sketch, "E368.0", {"start": v(21, 86.5) * mm, "end": v(29, 86.5) * mm});
            skLineSegment(sketch, "E369.0", {"start": v(29, 90.5) * mm, "end": v(29, 86.5) * mm});
            skLineSegment(sketch, "E370.0", {"start": v(21, 90.5) * mm, "end": v(29, 90.5) * mm});
            skLineSegment(sketch, "E371.0", {"start": v(-4, 90.5) * mm, "end": v(-4, 86.5) * mm});
            skLineSegment(sketch, "E372.0", {"start": v(-4, 86.5) * mm, "end": v(4, 86.5) * mm});
            skLineSegment(sketch, "E373.0", {"start": v(4, 90.5) * mm, "end": v(4, 86.5) * mm});
            skLineSegment(sketch, "E374.0", {"start": v(4, 90.5) * mm, "end": v(-4, 90.5) * mm});
            skLineSegment(sketch, "E375.0", {"start": v(-29, 90.5) * mm, "end": v(-29, 86.5) * mm});
            skLineSegment(sketch, "E376.0", {"start": v(-21, 86.5) * mm, "end": v(-29, 86.5) * mm});
            skLineSegment(sketch, "E377.0", {"start": v(-21, 90.5) * mm, "end": v(-21, 86.5) * mm});
            skLineSegment(sketch, "E378.0", {"start": v(-21, 90.5) * mm, "end": v(-29, 90.5) * mm});
            skLineSegment(sketch, "E379.0", {"start": v(-54, 90.5) * mm, "end": v(-54, 86.5) * mm});
            skLineSegment(sketch, "E380.0", {"start": v(-54, 86.5) * mm, "end": v(-46, 86.5) * mm});
            skLineSegment(sketch, "E381.0", {"start": v(-46, 90.5) * mm, "end": v(-46, 86.5) * mm});
            skLineSegment(sketch, "E382.0", {"start": v(-54, 90.5) * mm, "end": v(-46, 90.5) * mm});
            skSolve(sketch);
        }
        {
            var Q0;
            Q0=makeQuery(id+"F8.imprint","IMPRINT",FACE,{"disambiguationData":[TD([[makeQuery(id+"F8.imprint","IMPRINT",EDGE,{"derivedFrom":sQuery(id+"F8.wireOp",EDGE,"E336.0")}),1.0]])]});
            var Q1;
            Q1=makeQuery(id+"F7.imprint","IMPRINT",FACE,{"disambiguationData":[TD([[makeQuery(id+"F7.imprint","IMPRINT",EDGE,{"derivedFrom":sQuery(id+"F7.wireOp",EDGE,"E266.0")}),1.0]])]});
            var Q2;
            Q2=makeQuery(id+"F8.imprint","IMPRINT",FACE,{"disambiguationData":[TD([[makeQuery(id+"F8.imprint","IMPRINT",EDGE,{"derivedFrom":sQuery(id+"F8.wireOp",EDGE,"E339.0")}),1.0]])]});
            var Q3;
            Q3=makeQuery(id+"F7.imprint","IMPRINT",FACE,{"disambiguationData":[TD([[makeQuery(id+"F7.imprint","IMPRINT",EDGE,{"derivedFrom":sQuery(id+"F7.wireOp",EDGE,"E270.0")}),1.0]])]});
            var Q4;
            Q4=makeQuery(id+"F7.imprint","IMPRINT",FACE,{"disambiguationData":[TD([[makeQuery(id+"F7.imprint","IMPRINT",EDGE,{"derivedFrom":sQuery(id+"F7.wireOp",EDGE,"E274.0")}),1.0]])]});
            var Q5;
            Q5=makeQuery(id+"F8.imprint","IMPRINT",FACE,{"disambiguationData":[TD([[makeQuery(id+"F8.imprint","IMPRINT",EDGE,{"derivedFrom":sQuery(id+"F8.wireOp",EDGE,"E343.0")}),1.0]])]});
            var Q6;
            Q6=makeQuery(id+"F8.imprint","IMPRINT",FACE,{"disambiguationData":[TD([[makeQuery(id+"F8.imprint","IMPRINT",EDGE,{"derivedFrom":sQuery(id+"F8.wireOp",EDGE,"E347.0")}),1.0]])]});
            var Q7;
            Q7=makeQuery(id+"F8.imprint","IMPRINT",FACE,{"disambiguationData":[TD([[makeQuery(id+"F8.imprint","IMPRINT",EDGE,{"derivedFrom":sQuery(id+"F8.wireOp",EDGE,"E351.0")}),1.0]])]});
            var Q8;
            Q8=makeQuery(id+"F7.imprint","IMPRINT",FACE,{"disambiguationData":[TD([[makeQuery(id+"F7.imprint","IMPRINT",EDGE,{"derivedFrom":sQuery(id+"F7.wireOp",EDGE,"E278.0")}),-1.0]])]});
            var Q9;
            Q9=makeQuery(id+"F7.imprint","IMPRINT",FACE,{"disambiguationData":[TD([[makeQuery(id+"F7.imprint","IMPRINT",EDGE,{"derivedFrom":sQuery(id+"F7.wireOp",EDGE,"E282.0")}),1.0]])]});
            var Q10;
            Q10=makeQuery(id+"F8.imprint","IMPRINT",FACE,{"disambiguationData":[TD([[makeQuery(id+"F8.imprint","IMPRINT",EDGE,{"derivedFrom":sQuery(id+"F8.wireOp",EDGE,"E355.0")}),1.0]])]});
            var Q11;
            Q11=makeQuery(id+"F8.imprint","IMPRINT",FACE,{"disambiguationData":[TD([[makeQuery(id+"F8.imprint","IMPRINT",EDGE,{"derivedFrom":sQuery(id+"F8.wireOp",EDGE,"E359.0")}),1.0]])]});
            var Q12;
            Q12=makeQuery(id+"F7.imprint","IMPRINT",FACE,{"disambiguationData":[TD([[makeQuery(id+"F7.imprint","IMPRINT",EDGE,{"derivedFrom":sQuery(id+"F7.wireOp",EDGE,"E288.0")}),1.0]])]});
            var Q13;
            Q13=makeQuery(id+"F7.imprint","IMPRINT",FACE,{"disambiguationData":[TD([[makeQuery(id+"F7.imprint","IMPRINT",EDGE,{"derivedFrom":sQuery(id+"F7.wireOp",EDGE,"E292.0")}),1.0]])]});
            var Q14;
            Q14=makeQuery(id+"F8.imprint","IMPRINT",FACE,{"disambiguationData":[TD([[makeQuery(id+"F8.imprint","IMPRINT",EDGE,{"derivedFrom":sQuery(id+"F8.wireOp",EDGE,"E363.0")}),1.0]])]});
            var Q15;
            Q15=makeQuery(id+"F8.imprint","IMPRINT",FACE,{"disambiguationData":[TD([[makeQuery(id+"F8.imprint","IMPRINT",EDGE,{"derivedFrom":sQuery(id+"F8.wireOp",EDGE,"E367.0")}),1.0]])]});
            var Q16;
            Q16=makeQuery(id+"F8.imprint","IMPRINT",FACE,{"disambiguationData":[TD([[makeQuery(id+"F8.imprint","IMPRINT",EDGE,{"derivedFrom":sQuery(id+"F8.wireOp",EDGE,"E371.0")}),1.0]])]});
            var Q17;
            Q17=makeQuery(id+"F8.imprint","IMPRINT",FACE,{"disambiguationData":[TD([[makeQuery(id+"F8.imprint","IMPRINT",EDGE,{"derivedFrom":sQuery(id+"F8.wireOp",EDGE,"E375.0")}),1.0]])]});
            var Q18;
            Q18=makeQuery(id+"F8.imprint","IMPRINT",FACE,{"disambiguationData":[TD([[makeQuery(id+"F8.imprint","IMPRINT",EDGE,{"derivedFrom":sQuery(id+"F8.wireOp",EDGE,"E379.0")}),1.0]])]});
            var Q19;
            Q19=makeQuery(id+"F7.imprint","IMPRINT",FACE,{"disambiguationData":[TD([[makeQuery(id+"F7.imprint","IMPRINT",EDGE,{"derivedFrom":sQuery(id+"F7.wireOp",EDGE,"E311.0")}),1.0]])]});
            var Q20;
            Q20=makeQuery(id+"F7.imprint","IMPRINT",FACE,{"disambiguationData":[TD([[makeQuery(id+"F7.imprint","IMPRINT",EDGE,{"derivedFrom":sQuery(id+"F7.wireOp",EDGE,"E307.0")}),1.0]])]});
            var Q21;
            Q21=makeQuery(id+"F7.imprint","IMPRINT",FACE,{"disambiguationData":[TD([[makeQuery(id+"F7.imprint","IMPRINT",EDGE,{"derivedFrom":sQuery(id+"F7.wireOp",EDGE,"E303.0")}),1.0]])]});
            var Q22;
            Q22=makeQuery(id+"F7.imprint","IMPRINT",FACE,{"disambiguationData":[TD([[makeQuery(id+"F7.imprint","IMPRINT",EDGE,{"derivedFrom":sQuery(id+"F7.wireOp",EDGE,"E300.0")}),1.0]])]});
            var Q23;
            Q23=makeQuery(id+"F7.imprint","IMPRINT",FACE,{"disambiguationData":[TD([[makeQuery(id+"F7.imprint","IMPRINT",EDGE,{"derivedFrom":sQuery(id+"F7.wireOp",EDGE,"E296.0")}),1.0]])]});
            extrude(context, id + "F9", {"entities" : qUnion([Q0, Q1, Q2, Q3, Q4, Q5, Q6, Q7, Q8, Q9, Q10, Q11, Q12, Q13, Q14, Q15, Q16, Q17, Q18, Q19, Q20, Q21, Q22, Q23]), "oppositeDirection" : true, "depth" : 4 * mm});
        }
        {
            var Q0;
            Q0=makeQuery(id+"F9.opExtrude","CAP_FACE",FACE,{"disambiguationData":[OSD([sQuery(id+"F7.wireOp",EDGE,"E311.0"),sQuery(id+"F7.wireOp",EDGE,"E312.0"),sQuery(id+"F7.wireOp",EDGE,"E313.0"),sQuery(id+"F7.wireOp",EDGE,"E314.0")])],"isStart":true});
            var Q1;
            {var subQ5=makeQuery(id+"F1.opExtrude","CAP_EDGE",EDGE,{"disambiguationData":[OSD([sQuery(id+"F0.wireOp",EDGE,"E6.2.0.5")])],"isStart":false});Q1=makeQuery(id+"F5.imprint","IMPRINT",FACE,{"disambiguationData":[TD([[makeQuery(id+"F5.imprint","IMPRINT",EDGE,{"derivedFrom":subQ5}),1.0]])]});}
            var Q2;
            {var subQ1=makeQuery(id+"F1.opExtrude","CAP_EDGE",EDGE,{"disambiguationData":[OSD([sQuery(id+"F0.wireOp",EDGE,"E6.1.0.5")])],"isStart":false});Q2=makeQuery(id+"F5.imprint","IMPRINT",FACE,{"disambiguationData":[TD([[makeQuery(id+"F5.imprint","IMPRINT",EDGE,{"derivedFrom":subQ1}),1.0]])]});}
            var Q3;
            {var subQ1=makeQuery(id+"F1.opExtrude","CAP_EDGE",EDGE,{"disambiguationData":[OSD([sQuery(id+"F0.wireOp",EDGE,"E6.1.0.1")])],"isStart":false});Q3=makeQuery(id+"F5.imprint","IMPRINT",FACE,{"disambiguationData":[TD([[makeQuery(id+"F5.imprint","IMPRINT",EDGE,{"derivedFrom":subQ1}),1.0]])]});}
            var Q4;
            {var subQ1=makeQuery(id+"F1.opExtrude","CAP_EDGE",EDGE,{"disambiguationData":[OSD([sQuery(id+"F0.wireOp",EDGE,"E2.right")])],"isStart":false});Q4=makeQuery(id+"F5.imprint","IMPRINT",FACE,{"disambiguationData":[TD([[makeQuery(id+"F5.imprint","IMPRINT",EDGE,{"derivedFrom":subQ1}),1.0]])]});}
            var Q5;
            {var subQ1=makeQuery(id+"F1.opExtrude","CAP_EDGE",EDGE,{"disambiguationData":[OSD([sQuery(id+"F0.wireOp",EDGE,"E2.right")])],"isStart":false});Q5=makeQuery(id+"F5.imprint","IMPRINT",FACE,{"disambiguationData":[TD([[makeQuery(id+"F5.imprint","IMPRINT",EDGE,{"derivedFrom":subQ1}),-1.0]])]});}
            var Q6;
            {var subQ1=makeQuery(id+"F1.opExtrude","CAP_EDGE",EDGE,{"disambiguationData":[OSD([sQuery(id+"F0.wireOp",EDGE,"E3.MirrorCS")])],"isStart":false});Q6=makeQuery(id+"F5.imprint","IMPRINT",FACE,{"disambiguationData":[TD([[makeQuery(id+"F5.imprint","IMPRINT",EDGE,{"derivedFrom":subQ1}),-1.0]])]});}
            var Q7;
            {var subQ2=makeQuery(id+"F1.opExtrude","CAP_EDGE",EDGE,{"disambiguationData":[OSD([sQuery(id+"F0.wireOp",EDGE,"E9.MirrorCS")])],"isStart":false});Q7=makeQuery(id+"F5.imprint","IMPRINT",FACE,{"disambiguationData":[TD([[makeQuery(id+"F5.imprint","IMPRINT",EDGE,{"derivedFrom":subQ2}),1.0]])]});}
            var Q8;
            {var subQ0=sQuery(id+"F5.wireOp",EDGE,"E238.0");Q8=makeQuery(id+"F5.imprint","IMPRINT",FACE,{"disambiguationData":[TD([[makeQuery(id+"F5.imprint","IMPRINT",EDGE,{"derivedFrom":subQ0}),1.0]])]});}
            var Q9;
            {var subQ0=sQuery(id+"F5.wireOp",EDGE,"E238.0");Q9=makeQuery(id+"F5.imprint","IMPRINT",FACE,{"disambiguationData":[TD([[makeQuery(id+"F5.imprint","IMPRINT",EDGE,{"derivedFrom":subQ0}),-1.0]])]});}
            var Q10;
            {var subQ5=sQuery(id+"F5.wireOp",EDGE,"E239.0");Q10=makeQuery(id+"F5.imprint","IMPRINT",FACE,{"disambiguationData":[TD([[makeQuery(id+"F5.imprint","IMPRINT",EDGE,{"derivedFrom":subQ5}),-1.0]])]});}
            extrude(context, id + "F10", {"entities" : qUnion([Q0, Q1, Q2, Q3, Q4, Q5, Q6, Q7, Q8, Q9, Q10]), "depth" : 35 * mm});
        }
        {
            var Q0;
            Q0=makeQuery(id+"F6.opExtrude","SWEPT_BODY",BODY,{"disambiguationData":[OSD([sQuery(id+"F5.wireOp",EDGE,"E230.0.1"),sQuery(id+"F5.wireOp",EDGE,"E230.0.3"),sQuery(id+"F5.wireOp",EDGE,"E242"),sQuery(id+"F5.wireOp",EDGE,"E243")])]});
            var Q1;
            Q1=qCreatedBy(makeId("Right.planeOp"),FACE);
            mirror(context, id + "F11", {"entities" : qUnion([Q0]), "mirrorPlane" : qUnion([Q1])});
        }
        {
            var Q0;
            Q0=makeQuery(id+"F10.opExtrude","SWEPT_BODY",BODY,{"disambiguationData":[OSD([sQuery(id+"F0.wireOp",EDGE,"E6.2.0.1"),sQuery(id+"F5.wireOp",EDGE,"E235"),sQuery(id+"F5.wireOp",EDGE,"E244"),sQuery(id+"F5.wireOp",EDGE,"E245")])]});
            var Q1;
            Q1=qCreatedBy(makeId("Front.planeOp"),FACE);
            mirror(context, id + "F12", {"entities" : qUnion([Q0]), "mirrorPlane" : qUnion([Q1])});
        }
    });
